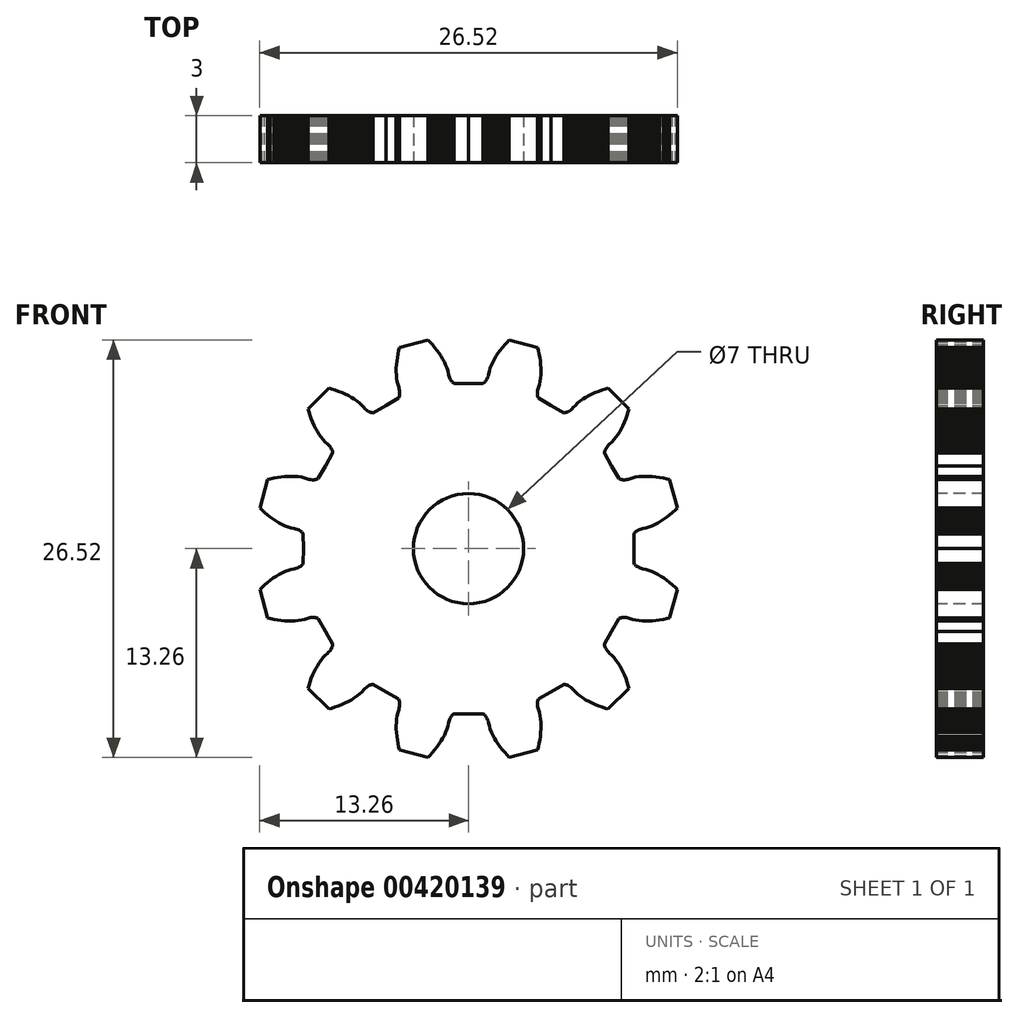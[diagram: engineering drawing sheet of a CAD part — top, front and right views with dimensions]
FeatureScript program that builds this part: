
annotation { "Feature Type Name" : "Feature", "Feature Type Description" : "" }
export const myFeature = defineFeature(function(context is Context, id is Id, definition is map)
    precondition{}
    {
        {
            var Q0;
            Q0=qCreatedBy(makeId("Front.planeOp"),FACE);
            var sketch = newSketch(context, id + "F0", { "sketchPlane" : qUnion([Q0])});
            skLineSegment(sketch, "E0", {"start": v(-10.5, 0) * mm, "end": v(-10.5, 0.93) * mm});
            skLineSegment(sketch, "E1", {"start": v(-10.5, 0.93) * mm, "end": v(-10.55, 1) * mm});
            skLineSegment(sketch, "E2", {"start": v(-10.55, 1) * mm, "end": v(-10.6, 1.05) * mm});
            skLineSegment(sketch, "E3", {"start": v(-10.6, 1.05) * mm, "end": v(-10.64, 1.09) * mm});
            skLineSegment(sketch, "E4", {"start": v(-10.64, 1.09) * mm, "end": v(-10.69, 1.12) * mm});
            skLineSegment(sketch, "E5", {"start": v(-10.69, 1.12) * mm, "end": v(-10.78, 1.17) * mm});
            skLineSegment(sketch, "E6", {"start": v(-10.78, 1.17) * mm, "end": v(-10.88, 1.22) * mm});
            skLineSegment(sketch, "E7", {"start": v(-10.88, 1.22) * mm, "end": v(-10.97, 1.25) * mm});
            skLineSegment(sketch, "E8", {"start": v(-10.97, 1.25) * mm, "end": v(-11.07, 1.28) * mm});
            skLineSegment(sketch, "E9", {"start": v(-11.07, 1.28) * mm, "end": v(-11.27, 1.32) * mm});
            skLineSegment(sketch, "E10", {"start": v(-11.27, 1.32) * mm, "end": v(-11.47, 1.38) * mm});
            skLineSegment(sketch, "E11", {"start": v(-11.47, 1.38) * mm, "end": v(-11.66, 1.45) * mm});
            skLineSegment(sketch, "E12", {"start": v(-11.66, 1.45) * mm, "end": v(-11.85, 1.54) * mm});
            skLineSegment(sketch, "E13", {"start": v(-11.85, 1.54) * mm, "end": v(-12.04, 1.64) * mm});
            skLineSegment(sketch, "E14", {"start": v(-12.04, 1.64) * mm, "end": v(-12.23, 1.76) * mm});
            skLineSegment(sketch, "E15", {"start": v(-12.23, 1.76) * mm, "end": v(-12.41, 1.88) * mm});
            skLineSegment(sketch, "E16", {"start": v(-12.41, 1.88) * mm, "end": v(-12.6, 2.01) * mm});
            skLineSegment(sketch, "E17", {"start": v(-12.6, 2.01) * mm, "end": v(-12.77, 2.15) * mm});
            skLineSegment(sketch, "E18", {"start": v(-12.77, 2.15) * mm, "end": v(-12.95, 2.3) * mm});
            skLineSegment(sketch, "E19", {"start": v(-12.95, 2.3) * mm, "end": v(-13.13, 2.46) * mm});
            skLineSegment(sketch, "E20", {"start": v(-13.13, 2.46) * mm, "end": v(-13.26, 2.58) * mm});
            skLineSegment(sketch, "E21", {"start": v(-13.26, 2.58) * mm, "end": v(-12.77, 4.4) * mm});
            skLineSegment(sketch, "E22", {"start": v(-12.77, 4.4) * mm, "end": v(-12.6, 4.43) * mm});
            skLineSegment(sketch, "E23", {"start": v(-12.6, 4.43) * mm, "end": v(-12.37, 4.48) * mm});
            skLineSegment(sketch, "E24", {"start": v(-12.37, 4.48) * mm, "end": v(-12.14, 4.52) * mm});
            skLineSegment(sketch, "E25", {"start": v(-12.14, 4.52) * mm, "end": v(-11.91, 4.56) * mm});
            skLineSegment(sketch, "E26", {"start": v(-11.91, 4.56) * mm, "end": v(-11.69, 4.58) * mm});
            skLineSegment(sketch, "E27", {"start": v(-11.69, 4.58) * mm, "end": v(-11.47, 4.6) * mm});
            skLineSegment(sketch, "E28", {"start": v(-11.47, 4.6) * mm, "end": v(-11.25, 4.6) * mm});
            skLineSegment(sketch, "E29", {"start": v(-11.25, 4.6) * mm, "end": v(-11.03, 4.59) * mm});
            skLineSegment(sketch, "E30", {"start": v(-11.03, 4.59) * mm, "end": v(-10.82, 4.57) * mm});
            skLineSegment(sketch, "E31", {"start": v(-10.82, 4.57) * mm, "end": v(-10.62, 4.54) * mm});
            skLineSegment(sketch, "E32", {"start": v(-10.62, 4.54) * mm, "end": v(-10.42, 4.5) * mm});
            skLineSegment(sketch, "E33", {"start": v(-10.42, 4.5) * mm, "end": v(-10.23, 4.43) * mm});
            skLineSegment(sketch, "E34", {"start": v(-10.23, 4.43) * mm, "end": v(-10.13, 4.4) * mm});
            skLineSegment(sketch, "E35", {"start": v(-10.13, 4.4) * mm, "end": v(-10.03, 4.38) * mm});
            skLineSegment(sketch, "E36", {"start": v(-10.03, 4.38) * mm, "end": v(-9.92, 4.37) * mm});
            skLineSegment(sketch, "E37", {"start": v(-9.92, 4.37) * mm, "end": v(-9.81, 4.37) * mm});
            skLineSegment(sketch, "E38", {"start": v(-9.81, 4.37) * mm, "end": v(-9.76, 4.38) * mm});
            skLineSegment(sketch, "E39", {"start": v(-9.76, 4.38) * mm, "end": v(-9.7, 4.39) * mm});
            skLineSegment(sketch, "E40", {"start": v(-9.7, 4.39) * mm, "end": v(-9.63, 4.4) * mm});
            skLineSegment(sketch, "E41", {"start": v(-9.63, 4.4) * mm, "end": v(-9.56, 4.44) * mm});
            skLineSegment(sketch, "E42", {"start": v(-9.56, 4.44) * mm, "end": v(-9.09, 5.25) * mm});
            skLineSegment(sketch, "E43", {"start": v(-9.09, 5.25) * mm, "end": v(-8.63, 6.06) * mm});
            skLineSegment(sketch, "E44", {"start": v(-8.63, 6.06) * mm, "end": v(-8.63, 6.14) * mm});
            skLineSegment(sketch, "E45", {"start": v(-8.63, 6.14) * mm, "end": v(-8.65, 6.2) * mm});
            skLineSegment(sketch, "E46", {"start": v(-8.65, 6.2) * mm, "end": v(-8.67, 6.26) * mm});
            skLineSegment(sketch, "E47", {"start": v(-8.67, 6.26) * mm, "end": v(-8.7, 6.31) * mm});
            skLineSegment(sketch, "E48", {"start": v(-8.7, 6.31) * mm, "end": v(-8.75, 6.4) * mm});
            skLineSegment(sketch, "E49", {"start": v(-8.75, 6.4) * mm, "end": v(-8.81, 6.5) * mm});
            skLineSegment(sketch, "E50", {"start": v(-8.81, 6.5) * mm, "end": v(-8.88, 6.57) * mm});
            skLineSegment(sketch, "E51", {"start": v(-8.88, 6.57) * mm, "end": v(-8.95, 6.64) * mm});
            skLineSegment(sketch, "E52", {"start": v(-8.95, 6.64) * mm, "end": v(-9.1, 6.78) * mm});
            skLineSegment(sketch, "E53", {"start": v(-9.1, 6.78) * mm, "end": v(-9.24, 6.92) * mm});
            skLineSegment(sketch, "E54", {"start": v(-9.24, 6.92) * mm, "end": v(-9.37, 7.09) * mm});
            skLineSegment(sketch, "E55", {"start": v(-9.37, 7.09) * mm, "end": v(-9.5, 7.26) * mm});
            skLineSegment(sketch, "E56", {"start": v(-9.5, 7.26) * mm, "end": v(-9.6, 7.44) * mm});
            skLineSegment(sketch, "E57", {"start": v(-9.6, 7.44) * mm, "end": v(-9.71, 7.63) * mm});
            skLineSegment(sketch, "E58", {"start": v(-9.71, 7.63) * mm, "end": v(-9.8, 7.83) * mm});
            skLineSegment(sketch, "E59", {"start": v(-9.8, 7.83) * mm, "end": v(-9.9, 8.04) * mm});
            skLineSegment(sketch, "E60", {"start": v(-9.9, 8.04) * mm, "end": v(-9.99, 8.25) * mm});
            skLineSegment(sketch, "E61", {"start": v(-9.99, 8.25) * mm, "end": v(-10.07, 8.47) * mm});
            skLineSegment(sketch, "E62", {"start": v(-10.07, 8.47) * mm, "end": v(-10.14, 8.7) * mm});
            skLineSegment(sketch, "E63", {"start": v(-10.14, 8.7) * mm, "end": v(-10.2, 8.87) * mm});
            skLineSegment(sketch, "E64", {"start": v(-10.2, 8.87) * mm, "end": v(-8.87, 10.2) * mm});
            skLineSegment(sketch, "E65", {"start": v(-8.87, 10.2) * mm, "end": v(-8.7, 10.14) * mm});
            skLineSegment(sketch, "E66", {"start": v(-8.7, 10.14) * mm, "end": v(-8.47, 10.07) * mm});
            skLineSegment(sketch, "E67", {"start": v(-8.47, 10.07) * mm, "end": v(-8.25, 9.99) * mm});
            skLineSegment(sketch, "E68", {"start": v(-8.25, 9.99) * mm, "end": v(-8.04, 9.9) * mm});
            skLineSegment(sketch, "E69", {"start": v(-8.04, 9.9) * mm, "end": v(-7.83, 9.8) * mm});
            skLineSegment(sketch, "E70", {"start": v(-7.83, 9.8) * mm, "end": v(-7.63, 9.71) * mm});
            skLineSegment(sketch, "E71", {"start": v(-7.63, 9.71) * mm, "end": v(-7.44, 9.6) * mm});
            skLineSegment(sketch, "E72", {"start": v(-7.44, 9.6) * mm, "end": v(-7.26, 9.5) * mm});
            skLineSegment(sketch, "E73", {"start": v(-7.26, 9.5) * mm, "end": v(-7.09, 9.37) * mm});
            skLineSegment(sketch, "E74", {"start": v(-7.09, 9.37) * mm, "end": v(-6.92, 9.24) * mm});
            skLineSegment(sketch, "E75", {"start": v(-6.92, 9.24) * mm, "end": v(-6.78, 9.1) * mm});
            skLineSegment(sketch, "E76", {"start": v(-6.78, 9.1) * mm, "end": v(-6.64, 8.95) * mm});
            skLineSegment(sketch, "E77", {"start": v(-6.64, 8.95) * mm, "end": v(-6.57, 8.88) * mm});
            skLineSegment(sketch, "E78", {"start": v(-6.57, 8.88) * mm, "end": v(-6.5, 8.81) * mm});
            skLineSegment(sketch, "E79", {"start": v(-6.5, 8.81) * mm, "end": v(-6.4, 8.75) * mm});
            skLineSegment(sketch, "E80", {"start": v(-6.4, 8.75) * mm, "end": v(-6.31, 8.7) * mm});
            skLineSegment(sketch, "E81", {"start": v(-6.31, 8.7) * mm, "end": v(-6.26, 8.67) * mm});
            skLineSegment(sketch, "E82", {"start": v(-6.26, 8.67) * mm, "end": v(-6.2, 8.65) * mm});
            skLineSegment(sketch, "E83", {"start": v(-6.2, 8.65) * mm, "end": v(-6.14, 8.63) * mm});
            skLineSegment(sketch, "E84", {"start": v(-6.14, 8.63) * mm, "end": v(-6.06, 8.63) * mm});
            skLineSegment(sketch, "E85", {"start": v(-6.06, 8.63) * mm, "end": v(-5.25, 9.09) * mm});
            skLineSegment(sketch, "E86", {"start": v(-5.25, 9.09) * mm, "end": v(-4.44, 9.56) * mm});
            skLineSegment(sketch, "E87", {"start": v(-4.44, 9.56) * mm, "end": v(-4.4, 9.63) * mm});
            skLineSegment(sketch, "E88", {"start": v(-4.4, 9.63) * mm, "end": v(-4.39, 9.7) * mm});
            skLineSegment(sketch, "E89", {"start": v(-4.39, 9.7) * mm, "end": v(-4.38, 9.76) * mm});
            skLineSegment(sketch, "E90", {"start": v(-4.38, 9.76) * mm, "end": v(-4.37, 9.81) * mm});
            skLineSegment(sketch, "E91", {"start": v(-4.37, 9.81) * mm, "end": v(-4.37, 9.92) * mm});
            skLineSegment(sketch, "E92", {"start": v(-4.37, 9.92) * mm, "end": v(-4.38, 10.03) * mm});
            skLineSegment(sketch, "E93", {"start": v(-4.38, 10.03) * mm, "end": v(-4.4, 10.13) * mm});
            skLineSegment(sketch, "E94", {"start": v(-4.4, 10.13) * mm, "end": v(-4.43, 10.23) * mm});
            skLineSegment(sketch, "E95", {"start": v(-4.43, 10.23) * mm, "end": v(-4.5, 10.42) * mm});
            skLineSegment(sketch, "E96", {"start": v(-4.5, 10.42) * mm, "end": v(-4.54, 10.62) * mm});
            skLineSegment(sketch, "E97", {"start": v(-4.54, 10.62) * mm, "end": v(-4.57, 10.82) * mm});
            skLineSegment(sketch, "E98", {"start": v(-4.57, 10.82) * mm, "end": v(-4.59, 11.03) * mm});
            skLineSegment(sketch, "E99", {"start": v(-4.59, 11.03) * mm, "end": v(-4.6, 11.25) * mm});
            skLineSegment(sketch, "E100", {"start": v(-4.6, 11.25) * mm, "end": v(-4.6, 11.47) * mm});
            skLineSegment(sketch, "E101", {"start": v(-4.6, 11.47) * mm, "end": v(-4.58, 11.69) * mm});
            skLineSegment(sketch, "E102", {"start": v(-4.58, 11.69) * mm, "end": v(-4.56, 11.91) * mm});
            skLineSegment(sketch, "E103", {"start": v(-4.56, 11.91) * mm, "end": v(-4.52, 12.14) * mm});
            skLineSegment(sketch, "E104", {"start": v(-4.52, 12.14) * mm, "end": v(-4.48, 12.37) * mm});
            skLineSegment(sketch, "E105", {"start": v(-4.48, 12.37) * mm, "end": v(-4.43, 12.6) * mm});
            skLineSegment(sketch, "E106", {"start": v(-4.43, 12.6) * mm, "end": v(-4.4, 12.77) * mm});
            skLineSegment(sketch, "E107", {"start": v(-4.4, 12.77) * mm, "end": v(-2.58, 13.26) * mm});
            skLineSegment(sketch, "E108", {"start": v(-2.58, 13.26) * mm, "end": v(-2.46, 13.13) * mm});
            skLineSegment(sketch, "E109", {"start": v(-2.46, 13.13) * mm, "end": v(-2.3, 12.95) * mm});
            skLineSegment(sketch, "E110", {"start": v(-2.3, 12.95) * mm, "end": v(-2.15, 12.77) * mm});
            skLineSegment(sketch, "E111", {"start": v(-2.15, 12.77) * mm, "end": v(-2.01, 12.6) * mm});
            skLineSegment(sketch, "E112", {"start": v(-2.01, 12.6) * mm, "end": v(-1.88, 12.41) * mm});
            skLineSegment(sketch, "E113", {"start": v(-1.88, 12.41) * mm, "end": v(-1.76, 12.23) * mm});
            skLineSegment(sketch, "E114", {"start": v(-1.76, 12.23) * mm, "end": v(-1.64, 12.04) * mm});
            skLineSegment(sketch, "E115", {"start": v(-1.64, 12.04) * mm, "end": v(-1.54, 11.85) * mm});
            skLineSegment(sketch, "E116", {"start": v(-1.54, 11.85) * mm, "end": v(-1.45, 11.66) * mm});
            skLineSegment(sketch, "E117", {"start": v(-1.45, 11.66) * mm, "end": v(-1.38, 11.47) * mm});
            skLineSegment(sketch, "E118", {"start": v(-1.38, 11.47) * mm, "end": v(-1.32, 11.27) * mm});
            skLineSegment(sketch, "E119", {"start": v(-1.32, 11.27) * mm, "end": v(-1.28, 11.07) * mm});
            skLineSegment(sketch, "E120", {"start": v(-1.28, 11.07) * mm, "end": v(-1.25, 10.97) * mm});
            skLineSegment(sketch, "E121", {"start": v(-1.25, 10.97) * mm, "end": v(-1.22, 10.88) * mm});
            skLineSegment(sketch, "E122", {"start": v(-1.22, 10.88) * mm, "end": v(-1.17, 10.78) * mm});
            skLineSegment(sketch, "E123", {"start": v(-1.17, 10.78) * mm, "end": v(-1.12, 10.69) * mm});
            skLineSegment(sketch, "E124", {"start": v(-1.12, 10.69) * mm, "end": v(-1.09, 10.64) * mm});
            skLineSegment(sketch, "E125", {"start": v(-1.09, 10.64) * mm, "end": v(-1.05, 10.6) * mm});
            skLineSegment(sketch, "E126", {"start": v(-1.05, 10.6) * mm, "end": v(-1, 10.55) * mm});
            skLineSegment(sketch, "E127", {"start": v(-1, 10.55) * mm, "end": v(-0.93, 10.5) * mm});
            skLineSegment(sketch, "E128", {"start": v(-0.93, 10.5) * mm, "end": v(0, 10.5) * mm});
            skLineSegment(sketch, "E129", {"start": v(0, 10.5) * mm, "end": v(0.93, 10.5) * mm});
            skLineSegment(sketch, "E130", {"start": v(0.93, 10.5) * mm, "end": v(1, 10.55) * mm});
            skLineSegment(sketch, "E131", {"start": v(1, 10.55) * mm, "end": v(1.05, 10.6) * mm});
            skLineSegment(sketch, "E132", {"start": v(1.05, 10.6) * mm, "end": v(1.09, 10.64) * mm});
            skLineSegment(sketch, "E133", {"start": v(1.09, 10.64) * mm, "end": v(1.12, 10.69) * mm});
            skLineSegment(sketch, "E134", {"start": v(1.12, 10.69) * mm, "end": v(1.17, 10.78) * mm});
            skLineSegment(sketch, "E135", {"start": v(1.17, 10.78) * mm, "end": v(1.22, 10.88) * mm});
            skLineSegment(sketch, "E136", {"start": v(1.22, 10.88) * mm, "end": v(1.25, 10.97) * mm});
            skLineSegment(sketch, "E137", {"start": v(1.25, 10.97) * mm, "end": v(1.28, 11.07) * mm});
            skLineSegment(sketch, "E138", {"start": v(1.28, 11.07) * mm, "end": v(1.32, 11.27) * mm});
            skLineSegment(sketch, "E139", {"start": v(1.32, 11.27) * mm, "end": v(1.38, 11.47) * mm});
            skLineSegment(sketch, "E140", {"start": v(1.38, 11.47) * mm, "end": v(1.45, 11.66) * mm});
            skLineSegment(sketch, "E141", {"start": v(1.45, 11.66) * mm, "end": v(1.54, 11.85) * mm});
            skLineSegment(sketch, "E142", {"start": v(1.54, 11.85) * mm, "end": v(1.64, 12.04) * mm});
            skLineSegment(sketch, "E143", {"start": v(1.64, 12.04) * mm, "end": v(1.76, 12.23) * mm});
            skLineSegment(sketch, "E144", {"start": v(1.76, 12.23) * mm, "end": v(1.88, 12.41) * mm});
            skLineSegment(sketch, "E145", {"start": v(1.88, 12.41) * mm, "end": v(2.01, 12.6) * mm});
            skLineSegment(sketch, "E146", {"start": v(2.01, 12.6) * mm, "end": v(2.15, 12.77) * mm});
            skLineSegment(sketch, "E147", {"start": v(2.15, 12.77) * mm, "end": v(2.3, 12.95) * mm});
            skLineSegment(sketch, "E148", {"start": v(2.3, 12.95) * mm, "end": v(2.46, 13.13) * mm});
            skLineSegment(sketch, "E149", {"start": v(2.46, 13.13) * mm, "end": v(2.58, 13.26) * mm});
            skLineSegment(sketch, "E150", {"start": v(2.58, 13.26) * mm, "end": v(4.4, 12.77) * mm});
            skLineSegment(sketch, "E151", {"start": v(4.4, 12.77) * mm, "end": v(4.43, 12.6) * mm});
            skLineSegment(sketch, "E152", {"start": v(4.43, 12.6) * mm, "end": v(4.48, 12.37) * mm});
            skLineSegment(sketch, "E153", {"start": v(4.48, 12.37) * mm, "end": v(4.52, 12.14) * mm});
            skLineSegment(sketch, "E154", {"start": v(4.52, 12.14) * mm, "end": v(4.56, 11.91) * mm});
            skLineSegment(sketch, "E155", {"start": v(4.56, 11.91) * mm, "end": v(4.58, 11.69) * mm});
            skLineSegment(sketch, "E156", {"start": v(4.58, 11.69) * mm, "end": v(4.6, 11.47) * mm});
            skLineSegment(sketch, "E157", {"start": v(4.6, 11.47) * mm, "end": v(4.6, 11.25) * mm});
            skLineSegment(sketch, "E158", {"start": v(4.6, 11.25) * mm, "end": v(4.59, 11.03) * mm});
            skLineSegment(sketch, "E159", {"start": v(4.59, 11.03) * mm, "end": v(4.57, 10.82) * mm});
            skLineSegment(sketch, "E160", {"start": v(4.57, 10.82) * mm, "end": v(4.54, 10.62) * mm});
            skLineSegment(sketch, "E161", {"start": v(4.54, 10.62) * mm, "end": v(4.5, 10.42) * mm});
            skLineSegment(sketch, "E162", {"start": v(4.5, 10.42) * mm, "end": v(4.43, 10.23) * mm});
            skLineSegment(sketch, "E163", {"start": v(4.43, 10.23) * mm, "end": v(4.4, 10.13) * mm});
            skLineSegment(sketch, "E164", {"start": v(4.4, 10.13) * mm, "end": v(4.38, 10.03) * mm});
            skLineSegment(sketch, "E165", {"start": v(4.38, 10.03) * mm, "end": v(4.37, 9.92) * mm});
            skLineSegment(sketch, "E166", {"start": v(4.37, 9.92) * mm, "end": v(4.37, 9.81) * mm});
            skLineSegment(sketch, "E167", {"start": v(4.37, 9.81) * mm, "end": v(4.38, 9.76) * mm});
            skLineSegment(sketch, "E168", {"start": v(4.38, 9.76) * mm, "end": v(4.39, 9.7) * mm});
            skLineSegment(sketch, "E169", {"start": v(4.39, 9.7) * mm, "end": v(4.4, 9.63) * mm});
            skLineSegment(sketch, "E170", {"start": v(4.4, 9.63) * mm, "end": v(4.44, 9.56) * mm});
            skLineSegment(sketch, "E171", {"start": v(4.44, 9.56) * mm, "end": v(5.25, 9.09) * mm});
            skLineSegment(sketch, "E172", {"start": v(5.25, 9.09) * mm, "end": v(6.06, 8.63) * mm});
            skLineSegment(sketch, "E173", {"start": v(6.06, 8.63) * mm, "end": v(6.14, 8.63) * mm});
            skLineSegment(sketch, "E174", {"start": v(6.14, 8.63) * mm, "end": v(6.2, 8.65) * mm});
            skLineSegment(sketch, "E175", {"start": v(6.2, 8.65) * mm, "end": v(6.26, 8.67) * mm});
            skLineSegment(sketch, "E176", {"start": v(6.26, 8.67) * mm, "end": v(6.31, 8.7) * mm});
            skLineSegment(sketch, "E177", {"start": v(6.31, 8.7) * mm, "end": v(6.4, 8.75) * mm});
            skLineSegment(sketch, "E178", {"start": v(6.4, 8.75) * mm, "end": v(6.5, 8.81) * mm});
            skLineSegment(sketch, "E179", {"start": v(6.5, 8.81) * mm, "end": v(6.57, 8.88) * mm});
            skLineSegment(sketch, "E180", {"start": v(6.57, 8.88) * mm, "end": v(6.64, 8.95) * mm});
            skLineSegment(sketch, "E181", {"start": v(6.64, 8.95) * mm, "end": v(6.78, 9.1) * mm});
            skLineSegment(sketch, "E182", {"start": v(6.78, 9.1) * mm, "end": v(6.92, 9.24) * mm});
            skLineSegment(sketch, "E183", {"start": v(6.92, 9.24) * mm, "end": v(7.09, 9.37) * mm});
            skLineSegment(sketch, "E184", {"start": v(7.09, 9.37) * mm, "end": v(7.26, 9.5) * mm});
            skLineSegment(sketch, "E185", {"start": v(7.26, 9.5) * mm, "end": v(7.44, 9.6) * mm});
            skLineSegment(sketch, "E186", {"start": v(7.44, 9.6) * mm, "end": v(7.63, 9.71) * mm});
            skLineSegment(sketch, "E187", {"start": v(7.63, 9.71) * mm, "end": v(7.83, 9.8) * mm});
            skLineSegment(sketch, "E188", {"start": v(7.83, 9.8) * mm, "end": v(8.04, 9.9) * mm});
            skLineSegment(sketch, "E189", {"start": v(8.04, 9.9) * mm, "end": v(8.25, 9.99) * mm});
            skLineSegment(sketch, "E190", {"start": v(8.25, 9.99) * mm, "end": v(8.47, 10.07) * mm});
            skLineSegment(sketch, "E191", {"start": v(8.47, 10.07) * mm, "end": v(8.7, 10.14) * mm});
            skLineSegment(sketch, "E192", {"start": v(8.7, 10.14) * mm, "end": v(8.87, 10.2) * mm});
            skLineSegment(sketch, "E193", {"start": v(8.87, 10.2) * mm, "end": v(10.19, 8.87) * mm});
            skLineSegment(sketch, "E194", {"start": v(10.19, 8.87) * mm, "end": v(10.14, 8.7) * mm});
            skLineSegment(sketch, "E195", {"start": v(10.14, 8.7) * mm, "end": v(10.07, 8.47) * mm});
            skLineSegment(sketch, "E196", {"start": v(10.07, 8.47) * mm, "end": v(9.99, 8.25) * mm});
            skLineSegment(sketch, "E197", {"start": v(9.99, 8.25) * mm, "end": v(9.9, 8.04) * mm});
            skLineSegment(sketch, "E198", {"start": v(9.9, 8.04) * mm, "end": v(9.8, 7.83) * mm});
            skLineSegment(sketch, "E199", {"start": v(9.8, 7.83) * mm, "end": v(9.71, 7.63) * mm});
            skLineSegment(sketch, "E200", {"start": v(9.71, 7.63) * mm, "end": v(9.6, 7.44) * mm});
            skLineSegment(sketch, "E201", {"start": v(9.6, 7.44) * mm, "end": v(9.5, 7.26) * mm});
            skLineSegment(sketch, "E202", {"start": v(9.5, 7.26) * mm, "end": v(9.37, 7.09) * mm});
            skLineSegment(sketch, "E203", {"start": v(9.37, 7.09) * mm, "end": v(9.24, 6.92) * mm});
            skLineSegment(sketch, "E204", {"start": v(9.24, 6.92) * mm, "end": v(9.1, 6.78) * mm});
            skLineSegment(sketch, "E205", {"start": v(9.1, 6.78) * mm, "end": v(8.95, 6.64) * mm});
            skLineSegment(sketch, "E206", {"start": v(8.95, 6.64) * mm, "end": v(8.88, 6.57) * mm});
            skLineSegment(sketch, "E207", {"start": v(8.88, 6.57) * mm, "end": v(8.81, 6.5) * mm});
            skLineSegment(sketch, "E208", {"start": v(8.81, 6.5) * mm, "end": v(8.75, 6.4) * mm});
            skLineSegment(sketch, "E209", {"start": v(8.75, 6.4) * mm, "end": v(8.7, 6.31) * mm});
            skLineSegment(sketch, "E210", {"start": v(8.7, 6.31) * mm, "end": v(8.67, 6.26) * mm});
            skLineSegment(sketch, "E211", {"start": v(8.67, 6.26) * mm, "end": v(8.65, 6.2) * mm});
            skLineSegment(sketch, "E212", {"start": v(8.65, 6.2) * mm, "end": v(8.63, 6.14) * mm});
            skLineSegment(sketch, "E213", {"start": v(8.63, 6.14) * mm, "end": v(8.63, 6.06) * mm});
            skLineSegment(sketch, "E214", {"start": v(8.63, 6.06) * mm, "end": v(9.09, 5.25) * mm});
            skLineSegment(sketch, "E215", {"start": v(9.09, 5.25) * mm, "end": v(9.56, 4.44) * mm});
            skLineSegment(sketch, "E216", {"start": v(9.56, 4.44) * mm, "end": v(9.63, 4.4) * mm});
            skLineSegment(sketch, "E217", {"start": v(9.63, 4.4) * mm, "end": v(9.7, 4.39) * mm});
            skLineSegment(sketch, "E218", {"start": v(9.7, 4.39) * mm, "end": v(9.76, 4.38) * mm});
            skLineSegment(sketch, "E219", {"start": v(9.76, 4.38) * mm, "end": v(9.81, 4.37) * mm});
            skLineSegment(sketch, "E220", {"start": v(9.81, 4.37) * mm, "end": v(9.92, 4.37) * mm});
            skLineSegment(sketch, "E221", {"start": v(9.92, 4.37) * mm, "end": v(10.03, 4.38) * mm});
            skLineSegment(sketch, "E222", {"start": v(10.03, 4.38) * mm, "end": v(10.13, 4.4) * mm});
            skLineSegment(sketch, "E223", {"start": v(10.13, 4.4) * mm, "end": v(10.23, 4.43) * mm});
            skLineSegment(sketch, "E224", {"start": v(10.23, 4.43) * mm, "end": v(10.42, 4.5) * mm});
            skLineSegment(sketch, "E225", {"start": v(10.42, 4.5) * mm, "end": v(10.62, 4.54) * mm});
            skLineSegment(sketch, "E226", {"start": v(10.62, 4.54) * mm, "end": v(10.82, 4.57) * mm});
            skLineSegment(sketch, "E227", {"start": v(10.82, 4.57) * mm, "end": v(11.03, 4.59) * mm});
            skLineSegment(sketch, "E228", {"start": v(11.03, 4.59) * mm, "end": v(11.25, 4.6) * mm});
            skLineSegment(sketch, "E229", {"start": v(11.25, 4.6) * mm, "end": v(11.47, 4.6) * mm});
            skLineSegment(sketch, "E230", {"start": v(11.47, 4.6) * mm, "end": v(11.69, 4.58) * mm});
            skLineSegment(sketch, "E231", {"start": v(11.69, 4.58) * mm, "end": v(11.91, 4.56) * mm});
            skLineSegment(sketch, "E232", {"start": v(11.91, 4.56) * mm, "end": v(12.14, 4.52) * mm});
            skLineSegment(sketch, "E233", {"start": v(12.14, 4.52) * mm, "end": v(12.37, 4.48) * mm});
            skLineSegment(sketch, "E234", {"start": v(12.37, 4.48) * mm, "end": v(12.6, 4.43) * mm});
            skLineSegment(sketch, "E235", {"start": v(12.6, 4.43) * mm, "end": v(12.77, 4.4) * mm});
            skLineSegment(sketch, "E236", {"start": v(12.77, 4.4) * mm, "end": v(13.26, 2.58) * mm});
            skLineSegment(sketch, "E237", {"start": v(13.26, 2.58) * mm, "end": v(13.13, 2.46) * mm});
            skLineSegment(sketch, "E238", {"start": v(13.13, 2.46) * mm, "end": v(12.95, 2.3) * mm});
            skLineSegment(sketch, "E239", {"start": v(12.95, 2.3) * mm, "end": v(12.77, 2.15) * mm});
            skLineSegment(sketch, "E240", {"start": v(12.77, 2.15) * mm, "end": v(12.6, 2.01) * mm});
            skLineSegment(sketch, "E241", {"start": v(12.6, 2.01) * mm, "end": v(12.41, 1.88) * mm});
            skLineSegment(sketch, "E242", {"start": v(12.41, 1.88) * mm, "end": v(12.23, 1.76) * mm});
            skLineSegment(sketch, "E243", {"start": v(12.23, 1.76) * mm, "end": v(12.04, 1.64) * mm});
            skLineSegment(sketch, "E244", {"start": v(12.04, 1.64) * mm, "end": v(11.85, 1.54) * mm});
            skLineSegment(sketch, "E245", {"start": v(11.85, 1.54) * mm, "end": v(11.66, 1.45) * mm});
            skLineSegment(sketch, "E246", {"start": v(11.66, 1.45) * mm, "end": v(11.47, 1.38) * mm});
            skLineSegment(sketch, "E247", {"start": v(11.47, 1.38) * mm, "end": v(11.27, 1.32) * mm});
            skLineSegment(sketch, "E248", {"start": v(11.27, 1.32) * mm, "end": v(11.07, 1.28) * mm});
            skLineSegment(sketch, "E249", {"start": v(11.07, 1.28) * mm, "end": v(10.97, 1.25) * mm});
            skLineSegment(sketch, "E250", {"start": v(10.97, 1.25) * mm, "end": v(10.88, 1.22) * mm});
            skLineSegment(sketch, "E251", {"start": v(10.88, 1.22) * mm, "end": v(10.78, 1.17) * mm});
            skLineSegment(sketch, "E252", {"start": v(10.78, 1.17) * mm, "end": v(10.69, 1.12) * mm});
            skLineSegment(sketch, "E253", {"start": v(10.69, 1.12) * mm, "end": v(10.64, 1.09) * mm});
            skLineSegment(sketch, "E254", {"start": v(10.64, 1.09) * mm, "end": v(10.6, 1.05) * mm});
            skLineSegment(sketch, "E255", {"start": v(10.6, 1.05) * mm, "end": v(10.55, 1) * mm});
            skLineSegment(sketch, "E256", {"start": v(10.55, 1) * mm, "end": v(10.5, 0.93) * mm});
            skLineSegment(sketch, "E257", {"start": v(10.5, 0.93) * mm, "end": v(10.5, 0) * mm});
            skLineSegment(sketch, "E258", {"start": v(10.5, 0) * mm, "end": v(10.5, -0.93) * mm});
            skLineSegment(sketch, "E259", {"start": v(10.5, -0.93) * mm, "end": v(10.55, -1) * mm});
            skLineSegment(sketch, "E260", {"start": v(10.55, -1) * mm, "end": v(10.6, -1.05) * mm});
            skLineSegment(sketch, "E261", {"start": v(10.6, -1.05) * mm, "end": v(10.64, -1.09) * mm});
            skLineSegment(sketch, "E262", {"start": v(10.64, -1.09) * mm, "end": v(10.69, -1.12) * mm});
            skLineSegment(sketch, "E263", {"start": v(10.69, -1.12) * mm, "end": v(10.78, -1.17) * mm});
            skLineSegment(sketch, "E264", {"start": v(10.78, -1.17) * mm, "end": v(10.88, -1.22) * mm});
            skLineSegment(sketch, "E265", {"start": v(10.88, -1.22) * mm, "end": v(10.97, -1.25) * mm});
            skLineSegment(sketch, "E266", {"start": v(10.97, -1.25) * mm, "end": v(11.07, -1.28) * mm});
            skLineSegment(sketch, "E267", {"start": v(11.07, -1.28) * mm, "end": v(11.27, -1.32) * mm});
            skLineSegment(sketch, "E268", {"start": v(11.27, -1.32) * mm, "end": v(11.47, -1.38) * mm});
            skLineSegment(sketch, "E269", {"start": v(11.47, -1.38) * mm, "end": v(11.66, -1.45) * mm});
            skLineSegment(sketch, "E270", {"start": v(11.66, -1.45) * mm, "end": v(11.85, -1.54) * mm});
            skLineSegment(sketch, "E271", {"start": v(11.85, -1.54) * mm, "end": v(12.04, -1.64) * mm});
            skLineSegment(sketch, "E272", {"start": v(12.04, -1.64) * mm, "end": v(12.23, -1.76) * mm});
            skLineSegment(sketch, "E273", {"start": v(12.23, -1.76) * mm, "end": v(12.41, -1.88) * mm});
            skLineSegment(sketch, "E274", {"start": v(12.41, -1.88) * mm, "end": v(12.6, -2.01) * mm});
            skLineSegment(sketch, "E275", {"start": v(12.6, -2.01) * mm, "end": v(12.77, -2.15) * mm});
            skLineSegment(sketch, "E276", {"start": v(12.77, -2.15) * mm, "end": v(12.95, -2.3) * mm});
            skLineSegment(sketch, "E277", {"start": v(12.95, -2.3) * mm, "end": v(13.13, -2.46) * mm});
            skLineSegment(sketch, "E278", {"start": v(13.13, -2.46) * mm, "end": v(13.26, -2.58) * mm});
            skLineSegment(sketch, "E279", {"start": v(13.26, -2.58) * mm, "end": v(12.77, -4.4) * mm});
            skLineSegment(sketch, "E280", {"start": v(12.77, -4.4) * mm, "end": v(12.6, -4.43) * mm});
            skLineSegment(sketch, "E281", {"start": v(12.6, -4.43) * mm, "end": v(12.37, -4.48) * mm});
            skLineSegment(sketch, "E282", {"start": v(12.37, -4.48) * mm, "end": v(12.14, -4.52) * mm});
            skLineSegment(sketch, "E283", {"start": v(12.14, -4.52) * mm, "end": v(11.91, -4.56) * mm});
            skLineSegment(sketch, "E284", {"start": v(11.91, -4.56) * mm, "end": v(11.69, -4.58) * mm});
            skLineSegment(sketch, "E285", {"start": v(11.69, -4.58) * mm, "end": v(11.47, -4.6) * mm});
            skLineSegment(sketch, "E286", {"start": v(11.47, -4.6) * mm, "end": v(11.25, -4.6) * mm});
            skLineSegment(sketch, "E287", {"start": v(11.25, -4.6) * mm, "end": v(11.03, -4.59) * mm});
            skLineSegment(sketch, "E288", {"start": v(11.03, -4.59) * mm, "end": v(10.82, -4.57) * mm});
            skLineSegment(sketch, "E289", {"start": v(10.82, -4.57) * mm, "end": v(10.62, -4.54) * mm});
            skLineSegment(sketch, "E290", {"start": v(10.62, -4.54) * mm, "end": v(10.42, -4.5) * mm});
            skLineSegment(sketch, "E291", {"start": v(10.42, -4.5) * mm, "end": v(10.23, -4.43) * mm});
            skLineSegment(sketch, "E292", {"start": v(10.23, -4.43) * mm, "end": v(10.13, -4.4) * mm});
            skLineSegment(sketch, "E293", {"start": v(10.13, -4.4) * mm, "end": v(10.03, -4.38) * mm});
            skLineSegment(sketch, "E294", {"start": v(10.03, -4.38) * mm, "end": v(9.92, -4.37) * mm});
            skLineSegment(sketch, "E295", {"start": v(9.92, -4.37) * mm, "end": v(9.81, -4.37) * mm});
            skLineSegment(sketch, "E296", {"start": v(9.81, -4.37) * mm, "end": v(9.76, -4.38) * mm});
            skLineSegment(sketch, "E297", {"start": v(9.76, -4.38) * mm, "end": v(9.7, -4.39) * mm});
            skLineSegment(sketch, "E298", {"start": v(9.7, -4.39) * mm, "end": v(9.63, -4.4) * mm});
            skLineSegment(sketch, "E299", {"start": v(9.63, -4.4) * mm, "end": v(9.56, -4.44) * mm});
            skLineSegment(sketch, "E300", {"start": v(9.56, -4.44) * mm, "end": v(9.09, -5.25) * mm});
            skLineSegment(sketch, "E301", {"start": v(9.09, -5.25) * mm, "end": v(8.63, -6.06) * mm});
            skLineSegment(sketch, "E302", {"start": v(8.63, -6.06) * mm, "end": v(8.63, -6.14) * mm});
            skLineSegment(sketch, "E303", {"start": v(8.63, -6.14) * mm, "end": v(8.65, -6.2) * mm});
            skLineSegment(sketch, "E304", {"start": v(8.65, -6.2) * mm, "end": v(8.67, -6.26) * mm});
            skLineSegment(sketch, "E305", {"start": v(8.67, -6.26) * mm, "end": v(8.7, -6.31) * mm});
            skLineSegment(sketch, "E306", {"start": v(8.7, -6.31) * mm, "end": v(8.75, -6.4) * mm});
            skLineSegment(sketch, "E307", {"start": v(8.75, -6.4) * mm, "end": v(8.81, -6.5) * mm});
            skLineSegment(sketch, "E308", {"start": v(8.81, -6.5) * mm, "end": v(8.88, -6.57) * mm});
            skLineSegment(sketch, "E309", {"start": v(8.88, -6.57) * mm, "end": v(8.95, -6.64) * mm});
            skLineSegment(sketch, "E310", {"start": v(8.95, -6.64) * mm, "end": v(9.1, -6.78) * mm});
            skLineSegment(sketch, "E311", {"start": v(9.1, -6.78) * mm, "end": v(9.24, -6.92) * mm});
            skLineSegment(sketch, "E312", {"start": v(9.24, -6.92) * mm, "end": v(9.37, -7.09) * mm});
            skLineSegment(sketch, "E313", {"start": v(9.37, -7.09) * mm, "end": v(9.5, -7.26) * mm});
            skLineSegment(sketch, "E314", {"start": v(9.5, -7.26) * mm, "end": v(9.6, -7.44) * mm});
            skLineSegment(sketch, "E315", {"start": v(9.6, -7.44) * mm, "end": v(9.71, -7.63) * mm});
            skLineSegment(sketch, "E316", {"start": v(9.71, -7.63) * mm, "end": v(9.8, -7.83) * mm});
            skLineSegment(sketch, "E317", {"start": v(9.8, -7.83) * mm, "end": v(9.9, -8.04) * mm});
            skLineSegment(sketch, "E318", {"start": v(9.9, -8.04) * mm, "end": v(9.99, -8.25) * mm});
            skLineSegment(sketch, "E319", {"start": v(9.99, -8.25) * mm, "end": v(10.07, -8.47) * mm});
            skLineSegment(sketch, "E320", {"start": v(10.07, -8.47) * mm, "end": v(10.14, -8.7) * mm});
            skLineSegment(sketch, "E321", {"start": v(10.14, -8.7) * mm, "end": v(10.19, -8.87) * mm});
            skLineSegment(sketch, "E322", {"start": v(10.19, -8.87) * mm, "end": v(8.87, -10.19) * mm});
            skLineSegment(sketch, "E323", {"start": v(8.87, -10.19) * mm, "end": v(8.7, -10.14) * mm});
            skLineSegment(sketch, "E324", {"start": v(8.7, -10.14) * mm, "end": v(8.47, -10.07) * mm});
            skLineSegment(sketch, "E325", {"start": v(8.47, -10.07) * mm, "end": v(8.25, -9.99) * mm});
            skLineSegment(sketch, "E326", {"start": v(8.25, -9.99) * mm, "end": v(8.04, -9.9) * mm});
            skLineSegment(sketch, "E327", {"start": v(8.04, -9.9) * mm, "end": v(7.83, -9.8) * mm});
            skLineSegment(sketch, "E328", {"start": v(7.83, -9.8) * mm, "end": v(7.63, -9.71) * mm});
            skLineSegment(sketch, "E329", {"start": v(7.63, -9.71) * mm, "end": v(7.44, -9.6) * mm});
            skLineSegment(sketch, "E330", {"start": v(7.44, -9.6) * mm, "end": v(7.26, -9.5) * mm});
            skLineSegment(sketch, "E331", {"start": v(7.26, -9.5) * mm, "end": v(7.09, -9.37) * mm});
            skLineSegment(sketch, "E332", {"start": v(7.09, -9.37) * mm, "end": v(6.92, -9.24) * mm});
            skLineSegment(sketch, "E333", {"start": v(6.92, -9.24) * mm, "end": v(6.78, -9.1) * mm});
            skLineSegment(sketch, "E334", {"start": v(6.78, -9.1) * mm, "end": v(6.64, -8.95) * mm});
            skLineSegment(sketch, "E335", {"start": v(6.64, -8.95) * mm, "end": v(6.57, -8.88) * mm});
            skLineSegment(sketch, "E336", {"start": v(6.57, -8.88) * mm, "end": v(6.5, -8.81) * mm});
            skLineSegment(sketch, "E337", {"start": v(6.5, -8.81) * mm, "end": v(6.4, -8.75) * mm});
            skLineSegment(sketch, "E338", {"start": v(6.4, -8.75) * mm, "end": v(6.31, -8.7) * mm});
            skLineSegment(sketch, "E339", {"start": v(6.31, -8.7) * mm, "end": v(6.26, -8.67) * mm});
            skLineSegment(sketch, "E340", {"start": v(6.26, -8.67) * mm, "end": v(6.2, -8.65) * mm});
            skLineSegment(sketch, "E341", {"start": v(6.2, -8.65) * mm, "end": v(6.14, -8.63) * mm});
            skLineSegment(sketch, "E342", {"start": v(6.14, -8.63) * mm, "end": v(6.06, -8.63) * mm});
            skLineSegment(sketch, "E343", {"start": v(6.06, -8.63) * mm, "end": v(5.25, -9.09) * mm});
            skLineSegment(sketch, "E344", {"start": v(5.25, -9.09) * mm, "end": v(4.44, -9.56) * mm});
            skLineSegment(sketch, "E345", {"start": v(4.44, -9.56) * mm, "end": v(4.4, -9.63) * mm});
            skLineSegment(sketch, "E346", {"start": v(4.4, -9.63) * mm, "end": v(4.39, -9.7) * mm});
            skLineSegment(sketch, "E347", {"start": v(4.39, -9.7) * mm, "end": v(4.38, -9.76) * mm});
            skLineSegment(sketch, "E348", {"start": v(4.38, -9.76) * mm, "end": v(4.37, -9.81) * mm});
            skLineSegment(sketch, "E349", {"start": v(4.37, -9.81) * mm, "end": v(4.37, -9.92) * mm});
            skLineSegment(sketch, "E350", {"start": v(4.37, -9.92) * mm, "end": v(4.38, -10.03) * mm});
            skLineSegment(sketch, "E351", {"start": v(4.38, -10.03) * mm, "end": v(4.4, -10.13) * mm});
            skLineSegment(sketch, "E352", {"start": v(4.4, -10.13) * mm, "end": v(4.43, -10.23) * mm});
            skLineSegment(sketch, "E353", {"start": v(4.43, -10.23) * mm, "end": v(4.5, -10.42) * mm});
            skLineSegment(sketch, "E354", {"start": v(4.5, -10.42) * mm, "end": v(4.54, -10.62) * mm});
            skLineSegment(sketch, "E355", {"start": v(4.54, -10.62) * mm, "end": v(4.57, -10.82) * mm});
            skLineSegment(sketch, "E356", {"start": v(4.57, -10.82) * mm, "end": v(4.59, -11.03) * mm});
            skLineSegment(sketch, "E357", {"start": v(4.59, -11.03) * mm, "end": v(4.6, -11.25) * mm});
            skLineSegment(sketch, "E358", {"start": v(4.6, -11.25) * mm, "end": v(4.6, -11.47) * mm});
            skLineSegment(sketch, "E359", {"start": v(4.6, -11.47) * mm, "end": v(4.58, -11.69) * mm});
            skLineSegment(sketch, "E360", {"start": v(4.58, -11.69) * mm, "end": v(4.56, -11.91) * mm});
            skLineSegment(sketch, "E361", {"start": v(4.56, -11.91) * mm, "end": v(4.52, -12.14) * mm});
            skLineSegment(sketch, "E362", {"start": v(4.52, -12.14) * mm, "end": v(4.48, -12.37) * mm});
            skLineSegment(sketch, "E363", {"start": v(4.48, -12.37) * mm, "end": v(4.43, -12.6) * mm});
            skLineSegment(sketch, "E364", {"start": v(4.43, -12.6) * mm, "end": v(4.4, -12.77) * mm});
            skLineSegment(sketch, "E365", {"start": v(4.4, -12.77) * mm, "end": v(2.58, -13.26) * mm});
            skLineSegment(sketch, "E366", {"start": v(2.58, -13.26) * mm, "end": v(2.46, -13.13) * mm});
            skLineSegment(sketch, "E367", {"start": v(2.46, -13.13) * mm, "end": v(2.3, -12.95) * mm});
            skLineSegment(sketch, "E368", {"start": v(2.3, -12.95) * mm, "end": v(2.15, -12.77) * mm});
            skLineSegment(sketch, "E369", {"start": v(2.15, -12.77) * mm, "end": v(2.01, -12.6) * mm});
            skLineSegment(sketch, "E370", {"start": v(2.01, -12.6) * mm, "end": v(1.88, -12.41) * mm});
            skLineSegment(sketch, "E371", {"start": v(1.88, -12.41) * mm, "end": v(1.76, -12.23) * mm});
            skLineSegment(sketch, "E372", {"start": v(1.76, -12.23) * mm, "end": v(1.64, -12.04) * mm});
            skLineSegment(sketch, "E373", {"start": v(1.64, -12.04) * mm, "end": v(1.54, -11.85) * mm});
            skLineSegment(sketch, "E374", {"start": v(1.54, -11.85) * mm, "end": v(1.45, -11.66) * mm});
            skLineSegment(sketch, "E375", {"start": v(1.45, -11.66) * mm, "end": v(1.38, -11.47) * mm});
            skLineSegment(sketch, "E376", {"start": v(1.38, -11.47) * mm, "end": v(1.32, -11.27) * mm});
            skLineSegment(sketch, "E377", {"start": v(1.32, -11.27) * mm, "end": v(1.28, -11.07) * mm});
            skLineSegment(sketch, "E378", {"start": v(1.28, -11.07) * mm, "end": v(1.25, -10.97) * mm});
            skLineSegment(sketch, "E379", {"start": v(1.25, -10.97) * mm, "end": v(1.22, -10.88) * mm});
            skLineSegment(sketch, "E380", {"start": v(1.22, -10.88) * mm, "end": v(1.17, -10.78) * mm});
            skLineSegment(sketch, "E381", {"start": v(1.17, -10.78) * mm, "end": v(1.12, -10.69) * mm});
            skLineSegment(sketch, "E382", {"start": v(1.12, -10.69) * mm, "end": v(1.09, -10.64) * mm});
            skLineSegment(sketch, "E383", {"start": v(1.09, -10.64) * mm, "end": v(1.05, -10.6) * mm});
            skLineSegment(sketch, "E384", {"start": v(1.05, -10.6) * mm, "end": v(1, -10.55) * mm});
            skLineSegment(sketch, "E385", {"start": v(1, -10.55) * mm, "end": v(0.93, -10.5) * mm});
            skLineSegment(sketch, "E386", {"start": v(0.93, -10.5) * mm, "end": v(0, -10.5) * mm});
            skLineSegment(sketch, "E387", {"start": v(0, -10.5) * mm, "end": v(-0.93, -10.5) * mm});
            skLineSegment(sketch, "E388", {"start": v(-0.93, -10.5) * mm, "end": v(-1, -10.55) * mm});
            skLineSegment(sketch, "E389", {"start": v(-1, -10.55) * mm, "end": v(-1.05, -10.6) * mm});
            skLineSegment(sketch, "E390", {"start": v(-1.05, -10.6) * mm, "end": v(-1.09, -10.64) * mm});
            skLineSegment(sketch, "E391", {"start": v(-1.09, -10.64) * mm, "end": v(-1.12, -10.69) * mm});
            skLineSegment(sketch, "E392", {"start": v(-1.12, -10.69) * mm, "end": v(-1.17, -10.78) * mm});
            skLineSegment(sketch, "E393", {"start": v(-1.17, -10.78) * mm, "end": v(-1.22, -10.88) * mm});
            skLineSegment(sketch, "E394", {"start": v(-1.22, -10.88) * mm, "end": v(-1.25, -10.97) * mm});
            skLineSegment(sketch, "E395", {"start": v(-1.25, -10.97) * mm, "end": v(-1.28, -11.07) * mm});
            skLineSegment(sketch, "E396", {"start": v(-1.28, -11.07) * mm, "end": v(-1.32, -11.27) * mm});
            skLineSegment(sketch, "E397", {"start": v(-1.32, -11.27) * mm, "end": v(-1.38, -11.47) * mm});
            skLineSegment(sketch, "E398", {"start": v(-1.38, -11.47) * mm, "end": v(-1.45, -11.66) * mm});
            skLineSegment(sketch, "E399", {"start": v(-1.45, -11.66) * mm, "end": v(-1.54, -11.85) * mm});
            skLineSegment(sketch, "E400", {"start": v(-1.54, -11.85) * mm, "end": v(-1.64, -12.04) * mm});
            skLineSegment(sketch, "E401", {"start": v(-1.64, -12.04) * mm, "end": v(-1.76, -12.23) * mm});
            skLineSegment(sketch, "E402", {"start": v(-1.76, -12.23) * mm, "end": v(-1.88, -12.41) * mm});
            skLineSegment(sketch, "E403", {"start": v(-1.88, -12.41) * mm, "end": v(-2.01, -12.6) * mm});
            skLineSegment(sketch, "E404", {"start": v(-2.01, -12.6) * mm, "end": v(-2.15, -12.77) * mm});
            skLineSegment(sketch, "E405", {"start": v(-2.15, -12.77) * mm, "end": v(-2.3, -12.95) * mm});
            skLineSegment(sketch, "E406", {"start": v(-2.3, -12.95) * mm, "end": v(-2.46, -13.13) * mm});
            skLineSegment(sketch, "E407", {"start": v(-2.46, -13.13) * mm, "end": v(-2.58, -13.26) * mm});
            skLineSegment(sketch, "E408", {"start": v(-2.58, -13.26) * mm, "end": v(-4.4, -12.77) * mm});
            skLineSegment(sketch, "E409", {"start": v(-4.4, -12.77) * mm, "end": v(-4.43, -12.6) * mm});
            skLineSegment(sketch, "E410", {"start": v(-4.43, -12.6) * mm, "end": v(-4.48, -12.37) * mm});
            skLineSegment(sketch, "E411", {"start": v(-4.48, -12.37) * mm, "end": v(-4.52, -12.14) * mm});
            skLineSegment(sketch, "E412", {"start": v(-4.52, -12.14) * mm, "end": v(-4.56, -11.91) * mm});
            skLineSegment(sketch, "E413", {"start": v(-4.56, -11.91) * mm, "end": v(-4.58, -11.69) * mm});
            skLineSegment(sketch, "E414", {"start": v(-4.58, -11.69) * mm, "end": v(-4.6, -11.47) * mm});
            skLineSegment(sketch, "E415", {"start": v(-4.6, -11.47) * mm, "end": v(-4.6, -11.25) * mm});
            skLineSegment(sketch, "E416", {"start": v(-4.6, -11.25) * mm, "end": v(-4.59, -11.03) * mm});
            skLineSegment(sketch, "E417", {"start": v(-4.59, -11.03) * mm, "end": v(-4.57, -10.82) * mm});
            skLineSegment(sketch, "E418", {"start": v(-4.57, -10.82) * mm, "end": v(-4.54, -10.62) * mm});
            skLineSegment(sketch, "E419", {"start": v(-4.54, -10.62) * mm, "end": v(-4.5, -10.42) * mm});
            skLineSegment(sketch, "E420", {"start": v(-4.5, -10.42) * mm, "end": v(-4.43, -10.23) * mm});
            skLineSegment(sketch, "E421", {"start": v(-4.43, -10.23) * mm, "end": v(-4.4, -10.13) * mm});
            skLineSegment(sketch, "E422", {"start": v(-4.4, -10.13) * mm, "end": v(-4.38, -10.03) * mm});
            skLineSegment(sketch, "E423", {"start": v(-4.38, -10.03) * mm, "end": v(-4.37, -9.92) * mm});
            skLineSegment(sketch, "E424", {"start": v(-4.37, -9.92) * mm, "end": v(-4.37, -9.81) * mm});
            skLineSegment(sketch, "E425", {"start": v(-4.37, -9.81) * mm, "end": v(-4.38, -9.76) * mm});
            skLineSegment(sketch, "E426", {"start": v(-4.38, -9.76) * mm, "end": v(-4.39, -9.7) * mm});
            skLineSegment(sketch, "E427", {"start": v(-4.39, -9.7) * mm, "end": v(-4.4, -9.63) * mm});
            skLineSegment(sketch, "E428", {"start": v(-4.4, -9.63) * mm, "end": v(-4.44, -9.56) * mm});
            skLineSegment(sketch, "E429", {"start": v(-4.44, -9.56) * mm, "end": v(-5.25, -9.09) * mm});
            skLineSegment(sketch, "E430", {"start": v(-5.25, -9.09) * mm, "end": v(-6.06, -8.63) * mm});
            skLineSegment(sketch, "E431", {"start": v(-6.06, -8.63) * mm, "end": v(-6.14, -8.63) * mm});
            skLineSegment(sketch, "E432", {"start": v(-6.14, -8.63) * mm, "end": v(-6.2, -8.65) * mm});
            skLineSegment(sketch, "E433", {"start": v(-6.2, -8.65) * mm, "end": v(-6.26, -8.67) * mm});
            skLineSegment(sketch, "E434", {"start": v(-6.26, -8.67) * mm, "end": v(-6.31, -8.7) * mm});
            skLineSegment(sketch, "E435", {"start": v(-6.31, -8.7) * mm, "end": v(-6.4, -8.75) * mm});
            skLineSegment(sketch, "E436", {"start": v(-6.4, -8.75) * mm, "end": v(-6.5, -8.81) * mm});
            skLineSegment(sketch, "E437", {"start": v(-6.5, -8.81) * mm, "end": v(-6.57, -8.88) * mm});
            skLineSegment(sketch, "E438", {"start": v(-6.57, -8.88) * mm, "end": v(-6.64, -8.95) * mm});
            skLineSegment(sketch, "E439", {"start": v(-6.64, -8.95) * mm, "end": v(-6.78, -9.1) * mm});
            skLineSegment(sketch, "E440", {"start": v(-6.78, -9.1) * mm, "end": v(-6.92, -9.24) * mm});
            skLineSegment(sketch, "E441", {"start": v(-6.92, -9.24) * mm, "end": v(-7.09, -9.37) * mm});
            skLineSegment(sketch, "E442", {"start": v(-7.09, -9.37) * mm, "end": v(-7.26, -9.5) * mm});
            skLineSegment(sketch, "E443", {"start": v(-7.26, -9.5) * mm, "end": v(-7.44, -9.6) * mm});
            skLineSegment(sketch, "E444", {"start": v(-7.44, -9.6) * mm, "end": v(-7.63, -9.71) * mm});
            skLineSegment(sketch, "E445", {"start": v(-7.63, -9.71) * mm, "end": v(-7.83, -9.8) * mm});
            skLineSegment(sketch, "E446", {"start": v(-7.83, -9.8) * mm, "end": v(-8.04, -9.9) * mm});
            skLineSegment(sketch, "E447", {"start": v(-8.04, -9.9) * mm, "end": v(-8.25, -9.99) * mm});
            skLineSegment(sketch, "E448", {"start": v(-8.25, -9.99) * mm, "end": v(-8.47, -10.07) * mm});
            skLineSegment(sketch, "E449", {"start": v(-8.47, -10.07) * mm, "end": v(-8.7, -10.14) * mm});
            skLineSegment(sketch, "E450", {"start": v(-8.7, -10.14) * mm, "end": v(-8.87, -10.19) * mm});
            skLineSegment(sketch, "E451", {"start": v(-8.87, -10.19) * mm, "end": v(-10.2, -8.87) * mm});
            skLineSegment(sketch, "E452", {"start": v(-10.2, -8.87) * mm, "end": v(-10.14, -8.7) * mm});
            skLineSegment(sketch, "E453", {"start": v(-10.14, -8.7) * mm, "end": v(-10.07, -8.47) * mm});
            skLineSegment(sketch, "E454", {"start": v(-10.07, -8.47) * mm, "end": v(-9.99, -8.25) * mm});
            skLineSegment(sketch, "E455", {"start": v(-9.99, -8.25) * mm, "end": v(-9.9, -8.04) * mm});
            skLineSegment(sketch, "E456", {"start": v(-9.9, -8.04) * mm, "end": v(-9.8, -7.83) * mm});
            skLineSegment(sketch, "E457", {"start": v(-9.8, -7.83) * mm, "end": v(-9.71, -7.63) * mm});
            skLineSegment(sketch, "E458", {"start": v(-9.71, -7.63) * mm, "end": v(-9.6, -7.44) * mm});
            skLineSegment(sketch, "E459", {"start": v(-9.6, -7.44) * mm, "end": v(-9.5, -7.26) * mm});
            skLineSegment(sketch, "E460", {"start": v(-9.5, -7.26) * mm, "end": v(-9.37, -7.09) * mm});
            skLineSegment(sketch, "E461", {"start": v(-9.37, -7.09) * mm, "end": v(-9.24, -6.92) * mm});
            skLineSegment(sketch, "E462", {"start": v(-9.24, -6.92) * mm, "end": v(-9.1, -6.78) * mm});
            skLineSegment(sketch, "E463", {"start": v(-9.1, -6.78) * mm, "end": v(-8.95, -6.64) * mm});
            skLineSegment(sketch, "E464", {"start": v(-8.95, -6.64) * mm, "end": v(-8.88, -6.57) * mm});
            skLineSegment(sketch, "E465", {"start": v(-8.88, -6.57) * mm, "end": v(-8.81, -6.5) * mm});
            skLineSegment(sketch, "E466", {"start": v(-8.81, -6.5) * mm, "end": v(-8.75, -6.4) * mm});
            skLineSegment(sketch, "E467", {"start": v(-8.75, -6.4) * mm, "end": v(-8.7, -6.31) * mm});
            skLineSegment(sketch, "E468", {"start": v(-8.7, -6.31) * mm, "end": v(-8.67, -6.26) * mm});
            skLineSegment(sketch, "E469", {"start": v(-8.67, -6.26) * mm, "end": v(-8.65, -6.2) * mm});
            skLineSegment(sketch, "E470", {"start": v(-8.65, -6.2) * mm, "end": v(-8.63, -6.14) * mm});
            skLineSegment(sketch, "E471", {"start": v(-8.63, -6.14) * mm, "end": v(-8.63, -6.06) * mm});
            skLineSegment(sketch, "E472", {"start": v(-8.63, -6.06) * mm, "end": v(-9.09, -5.25) * mm});
            skLineSegment(sketch, "E473", {"start": v(-9.09, -5.25) * mm, "end": v(-9.56, -4.44) * mm});
            skLineSegment(sketch, "E474", {"start": v(-9.56, -4.44) * mm, "end": v(-9.63, -4.4) * mm});
            skLineSegment(sketch, "E475", {"start": v(-9.63, -4.4) * mm, "end": v(-9.7, -4.39) * mm});
            skLineSegment(sketch, "E476", {"start": v(-9.7, -4.39) * mm, "end": v(-9.76, -4.38) * mm});
            skLineSegment(sketch, "E477", {"start": v(-9.76, -4.38) * mm, "end": v(-9.81, -4.37) * mm});
            skLineSegment(sketch, "E478", {"start": v(-9.81, -4.37) * mm, "end": v(-9.92, -4.37) * mm});
            skLineSegment(sketch, "E479", {"start": v(-9.92, -4.37) * mm, "end": v(-10.03, -4.38) * mm});
            skLineSegment(sketch, "E480", {"start": v(-10.03, -4.38) * mm, "end": v(-10.13, -4.4) * mm});
            skLineSegment(sketch, "E481", {"start": v(-10.13, -4.4) * mm, "end": v(-10.23, -4.43) * mm});
            skLineSegment(sketch, "E482", {"start": v(-10.23, -4.43) * mm, "end": v(-10.42, -4.5) * mm});
            skLineSegment(sketch, "E483", {"start": v(-10.42, -4.5) * mm, "end": v(-10.62, -4.54) * mm});
            skLineSegment(sketch, "E484", {"start": v(-10.62, -4.54) * mm, "end": v(-10.82, -4.57) * mm});
            skLineSegment(sketch, "E485", {"start": v(-10.82, -4.57) * mm, "end": v(-11.03, -4.59) * mm});
            skLineSegment(sketch, "E486", {"start": v(-11.03, -4.59) * mm, "end": v(-11.25, -4.6) * mm});
            skLineSegment(sketch, "E487", {"start": v(-11.25, -4.6) * mm, "end": v(-11.47, -4.6) * mm});
            skLineSegment(sketch, "E488", {"start": v(-11.47, -4.6) * mm, "end": v(-11.69, -4.58) * mm});
            skLineSegment(sketch, "E489", {"start": v(-11.69, -4.58) * mm, "end": v(-11.91, -4.56) * mm});
            skLineSegment(sketch, "E490", {"start": v(-11.91, -4.56) * mm, "end": v(-12.14, -4.52) * mm});
            skLineSegment(sketch, "E491", {"start": v(-12.14, -4.52) * mm, "end": v(-12.37, -4.48) * mm});
            skLineSegment(sketch, "E492", {"start": v(-12.37, -4.48) * mm, "end": v(-12.6, -4.43) * mm});
            skLineSegment(sketch, "E493", {"start": v(-12.6, -4.43) * mm, "end": v(-12.77, -4.4) * mm});
            skLineSegment(sketch, "E494", {"start": v(-12.77, -4.4) * mm, "end": v(-13.26, -2.58) * mm});
            skLineSegment(sketch, "E495", {"start": v(-13.26, -2.58) * mm, "end": v(-13.13, -2.46) * mm});
            skLineSegment(sketch, "E496", {"start": v(-13.13, -2.46) * mm, "end": v(-12.95, -2.3) * mm});
            skLineSegment(sketch, "E497", {"start": v(-12.95, -2.3) * mm, "end": v(-12.77, -2.15) * mm});
            skLineSegment(sketch, "E498", {"start": v(-12.77, -2.15) * mm, "end": v(-12.6, -2.01) * mm});
            skLineSegment(sketch, "E499", {"start": v(-12.6, -2.01) * mm, "end": v(-12.41, -1.88) * mm});
            skLineSegment(sketch, "E500", {"start": v(-12.41, -1.88) * mm, "end": v(-12.23, -1.76) * mm});
            skLineSegment(sketch, "E501", {"start": v(-12.23, -1.76) * mm, "end": v(-12.04, -1.64) * mm});
            skLineSegment(sketch, "E502", {"start": v(-12.04, -1.64) * mm, "end": v(-11.85, -1.54) * mm});
            skLineSegment(sketch, "E503", {"start": v(-11.85, -1.54) * mm, "end": v(-11.66, -1.45) * mm});
            skLineSegment(sketch, "E504", {"start": v(-11.66, -1.45) * mm, "end": v(-11.47, -1.38) * mm});
            skLineSegment(sketch, "E505", {"start": v(-11.47, -1.38) * mm, "end": v(-11.27, -1.32) * mm});
            skLineSegment(sketch, "E506", {"start": v(-11.27, -1.32) * mm, "end": v(-11.07, -1.28) * mm});
            skLineSegment(sketch, "E507", {"start": v(-11.07, -1.28) * mm, "end": v(-10.97, -1.25) * mm});
            skLineSegment(sketch, "E508", {"start": v(-10.97, -1.25) * mm, "end": v(-10.88, -1.22) * mm});
            skLineSegment(sketch, "E509", {"start": v(-10.88, -1.22) * mm, "end": v(-10.78, -1.17) * mm});
            skLineSegment(sketch, "E510", {"start": v(-10.78, -1.17) * mm, "end": v(-10.69, -1.12) * mm});
            skLineSegment(sketch, "E511", {"start": v(-10.69, -1.12) * mm, "end": v(-10.64, -1.09) * mm});
            skLineSegment(sketch, "E512", {"start": v(-10.64, -1.09) * mm, "end": v(-10.6, -1.05) * mm});
            skLineSegment(sketch, "E513", {"start": v(-10.6, -1.05) * mm, "end": v(-10.55, -1) * mm});
            skLineSegment(sketch, "E514", {"start": v(-10.55, -1) * mm, "end": v(-10.5, -0.93) * mm});
            skLineSegment(sketch, "E515", {"start": v(-10.5, -0.93) * mm, "end": v(-10.5, 0) * mm});
            skPoint(sketch, "E516", {"position": v(0, 0) * mm});
            skSolve(sketch);
        }
        {
            var Q0;
            Q0=makeQuery(id+"F0.imprint","IMPRINT",FACE,{"disambiguationData":[TD([[makeQuery(id+"F0.imprint","IMPRINT",EDGE,{"derivedFrom":sQuery(id+"F0.wireOp",EDGE,"E0")}),-1.0]])]});
            extrude(context, id + "F1", {"entities" : qUnion([Q0]), "depth" : 3 * mm});
        }
        {
            var Q0;
            Q0=makeQuery(id+"F1.opExtrude","CAP_FACE",FACE,{"disambiguationData":[OSD([sQuery(id+"F0.wireOp",EDGE,"E0"),sQuery(id+"F0.wireOp",EDGE,"E1"),sQuery(id+"F0.wireOp",EDGE,"E2"),sQuery(id+"F0.wireOp",EDGE,"E3"),sQuery(id+"F0.wireOp",EDGE,"E4"),sQuery(id+"F0.wireOp",EDGE,"E5"),sQuery(id+"F0.wireOp",EDGE,"E6"),sQuery(id+"F0.wireOp",EDGE,"E7"),sQuery(id+"F0.wireOp",EDGE,"E8"),sQuery(id+"F0.wireOp",EDGE,"E9"),sQuery(id+"F0.wireOp",EDGE,"E10"),sQuery(id+"F0.wireOp",EDGE,"E11"),sQuery(id+"F0.wireOp",EDGE,"E12"),sQuery(id+"F0.wireOp",EDGE,"E13"),sQuery(id+"F0.wireOp",EDGE,"E14"),sQuery(id+"F0.wireOp",EDGE,"E15"),sQuery(id+"F0.wireOp",EDGE,"E16"),sQuery(id+"F0.wireOp",EDGE,"E17"),sQuery(id+"F0.wireOp",EDGE,"E18"),sQuery(id+"F0.wireOp",EDGE,"E19"),sQuery(id+"F0.wireOp",EDGE,"E20"),sQuery(id+"F0.wireOp",EDGE,"E21"),sQuery(id+"F0.wireOp",EDGE,"E22"),sQuery(id+"F0.wireOp",EDGE,"E23"),sQuery(id+"F0.wireOp",EDGE,"E24"),sQuery(id+"F0.wireOp",EDGE,"E25"),sQuery(id+"F0.wireOp",EDGE,"E26"),sQuery(id+"F0.wireOp",EDGE,"E27"),sQuery(id+"F0.wireOp",EDGE,"E28"),sQuery(id+"F0.wireOp",EDGE,"E29"),sQuery(id+"F0.wireOp",EDGE,"E30"),sQuery(id+"F0.wireOp",EDGE,"E31"),sQuery(id+"F0.wireOp",EDGE,"E32"),sQuery(id+"F0.wireOp",EDGE,"E33"),sQuery(id+"F0.wireOp",EDGE,"E34"),sQuery(id+"F0.wireOp",EDGE,"E35"),sQuery(id+"F0.wireOp",EDGE,"E36"),sQuery(id+"F0.wireOp",EDGE,"E37"),sQuery(id+"F0.wireOp",EDGE,"E38"),sQuery(id+"F0.wireOp",EDGE,"E39"),sQuery(id+"F0.wireOp",EDGE,"E40"),sQuery(id+"F0.wireOp",EDGE,"E41"),sQuery(id+"F0.wireOp",EDGE,"E42"),sQuery(id+"F0.wireOp",EDGE,"E43"),sQuery(id+"F0.wireOp",EDGE,"E44"),sQuery(id+"F0.wireOp",EDGE,"E45"),sQuery(id+"F0.wireOp",EDGE,"E46"),sQuery(id+"F0.wireOp",EDGE,"E47"),sQuery(id+"F0.wireOp",EDGE,"E48"),sQuery(id+"F0.wireOp",EDGE,"E49"),sQuery(id+"F0.wireOp",EDGE,"E50"),sQuery(id+"F0.wireOp",EDGE,"E51"),sQuery(id+"F0.wireOp",EDGE,"E52"),sQuery(id+"F0.wireOp",EDGE,"E53"),sQuery(id+"F0.wireOp",EDGE,"E54"),sQuery(id+"F0.wireOp",EDGE,"E55"),sQuery(id+"F0.wireOp",EDGE,"E56"),sQuery(id+"F0.wireOp",EDGE,"E57"),sQuery(id+"F0.wireOp",EDGE,"E58"),sQuery(id+"F0.wireOp",EDGE,"E59"),sQuery(id+"F0.wireOp",EDGE,"E60"),sQuery(id+"F0.wireOp",EDGE,"E61"),sQuery(id+"F0.wireOp",EDGE,"E62"),sQuery(id+"F0.wireOp",EDGE,"E63"),sQuery(id+"F0.wireOp",EDGE,"E64"),sQuery(id+"F0.wireOp",EDGE,"E65"),sQuery(id+"F0.wireOp",EDGE,"E66"),sQuery(id+"F0.wireOp",EDGE,"E67"),sQuery(id+"F0.wireOp",EDGE,"E68"),sQuery(id+"F0.wireOp",EDGE,"E69"),sQuery(id+"F0.wireOp",EDGE,"E70"),sQuery(id+"F0.wireOp",EDGE,"E71"),sQuery(id+"F0.wireOp",EDGE,"E72"),sQuery(id+"F0.wireOp",EDGE,"E73"),sQuery(id+"F0.wireOp",EDGE,"E74"),sQuery(id+"F0.wireOp",EDGE,"E75"),sQuery(id+"F0.wireOp",EDGE,"E76"),sQuery(id+"F0.wireOp",EDGE,"E77"),sQuery(id+"F0.wireOp",EDGE,"E78"),sQuery(id+"F0.wireOp",EDGE,"E79"),sQuery(id+"F0.wireOp",EDGE,"E80"),sQuery(id+"F0.wireOp",EDGE,"E81"),sQuery(id+"F0.wireOp",EDGE,"E82"),sQuery(id+"F0.wireOp",EDGE,"E83"),sQuery(id+"F0.wireOp",EDGE,"E84"),sQuery(id+"F0.wireOp",EDGE,"E85"),sQuery(id+"F0.wireOp",EDGE,"E86"),sQuery(id+"F0.wireOp",EDGE,"E87"),sQuery(id+"F0.wireOp",EDGE,"E88"),sQuery(id+"F0.wireOp",EDGE,"E89"),sQuery(id+"F0.wireOp",EDGE,"E90"),sQuery(id+"F0.wireOp",EDGE,"E91"),sQuery(id+"F0.wireOp",EDGE,"E92"),sQuery(id+"F0.wireOp",EDGE,"E93"),sQuery(id+"F0.wireOp",EDGE,"E94"),sQuery(id+"F0.wireOp",EDGE,"E95"),sQuery(id+"F0.wireOp",EDGE,"E96"),sQuery(id+"F0.wireOp",EDGE,"E97"),sQuery(id+"F0.wireOp",EDGE,"E98"),sQuery(id+"F0.wireOp",EDGE,"E99"),sQuery(id+"F0.wireOp",EDGE,"E100"),sQuery(id+"F0.wireOp",EDGE,"E101"),sQuery(id+"F0.wireOp",EDGE,"E102"),sQuery(id+"F0.wireOp",EDGE,"E103"),sQuery(id+"F0.wireOp",EDGE,"E104"),sQuery(id+"F0.wireOp",EDGE,"E105"),sQuery(id+"F0.wireOp",EDGE,"E106"),sQuery(id+"F0.wireOp",EDGE,"E107"),sQuery(id+"F0.wireOp",EDGE,"E108"),sQuery(id+"F0.wireOp",EDGE,"E109"),sQuery(id+"F0.wireOp",EDGE,"E110"),sQuery(id+"F0.wireOp",EDGE,"E111"),sQuery(id+"F0.wireOp",EDGE,"E112"),sQuery(id+"F0.wireOp",EDGE,"E113"),sQuery(id+"F0.wireOp",EDGE,"E114"),sQuery(id+"F0.wireOp",EDGE,"E115"),sQuery(id+"F0.wireOp",EDGE,"E116"),sQuery(id+"F0.wireOp",EDGE,"E117"),sQuery(id+"F0.wireOp",EDGE,"E118"),sQuery(id+"F0.wireOp",EDGE,"E119"),sQuery(id+"F0.wireOp",EDGE,"E120"),sQuery(id+"F0.wireOp",EDGE,"E121"),sQuery(id+"F0.wireOp",EDGE,"E122"),sQuery(id+"F0.wireOp",EDGE,"E123"),sQuery(id+"F0.wireOp",EDGE,"E124"),sQuery(id+"F0.wireOp",EDGE,"E125"),sQuery(id+"F0.wireOp",EDGE,"E126"),sQuery(id+"F0.wireOp",EDGE,"E127"),sQuery(id+"F0.wireOp",EDGE,"E128"),sQuery(id+"F0.wireOp",EDGE,"E129"),sQuery(id+"F0.wireOp",EDGE,"E130"),sQuery(id+"F0.wireOp",EDGE,"E131"),sQuery(id+"F0.wireOp",EDGE,"E132"),sQuery(id+"F0.wireOp",EDGE,"E133"),sQuery(id+"F0.wireOp",EDGE,"E134"),sQuery(id+"F0.wireOp",EDGE,"E135"),sQuery(id+"F0.wireOp",EDGE,"E136"),sQuery(id+"F0.wireOp",EDGE,"E137"),sQuery(id+"F0.wireOp",EDGE,"E138"),sQuery(id+"F0.wireOp",EDGE,"E139"),sQuery(id+"F0.wireOp",EDGE,"E140"),sQuery(id+"F0.wireOp",EDGE,"E141"),sQuery(id+"F0.wireOp",EDGE,"E142"),sQuery(id+"F0.wireOp",EDGE,"E143"),sQuery(id+"F0.wireOp",EDGE,"E144"),sQuery(id+"F0.wireOp",EDGE,"E145"),sQuery(id+"F0.wireOp",EDGE,"E146"),sQuery(id+"F0.wireOp",EDGE,"E147"),sQuery(id+"F0.wireOp",EDGE,"E148"),sQuery(id+"F0.wireOp",EDGE,"E149"),sQuery(id+"F0.wireOp",EDGE,"E150"),sQuery(id+"F0.wireOp",EDGE,"E151"),sQuery(id+"F0.wireOp",EDGE,"E152"),sQuery(id+"F0.wireOp",EDGE,"E153"),sQuery(id+"F0.wireOp",EDGE,"E154"),sQuery(id+"F0.wireOp",EDGE,"E155"),sQuery(id+"F0.wireOp",EDGE,"E156"),sQuery(id+"F0.wireOp",EDGE,"E157"),sQuery(id+"F0.wireOp",EDGE,"E158"),sQuery(id+"F0.wireOp",EDGE,"E159"),sQuery(id+"F0.wireOp",EDGE,"E160"),sQuery(id+"F0.wireOp",EDGE,"E161"),sQuery(id+"F0.wireOp",EDGE,"E162"),sQuery(id+"F0.wireOp",EDGE,"E163"),sQuery(id+"F0.wireOp",EDGE,"E164"),sQuery(id+"F0.wireOp",EDGE,"E165"),sQuery(id+"F0.wireOp",EDGE,"E166"),sQuery(id+"F0.wireOp",EDGE,"E167"),sQuery(id+"F0.wireOp",EDGE,"E168"),sQuery(id+"F0.wireOp",EDGE,"E169"),sQuery(id+"F0.wireOp",EDGE,"E170"),sQuery(id+"F0.wireOp",EDGE,"E171"),sQuery(id+"F0.wireOp",EDGE,"E172"),sQuery(id+"F0.wireOp",EDGE,"E173"),sQuery(id+"F0.wireOp",EDGE,"E174"),sQuery(id+"F0.wireOp",EDGE,"E175"),sQuery(id+"F0.wireOp",EDGE,"E176"),sQuery(id+"F0.wireOp",EDGE,"E177"),sQuery(id+"F0.wireOp",EDGE,"E178"),sQuery(id+"F0.wireOp",EDGE,"E179"),sQuery(id+"F0.wireOp",EDGE,"E180"),sQuery(id+"F0.wireOp",EDGE,"E181"),sQuery(id+"F0.wireOp",EDGE,"E182"),sQuery(id+"F0.wireOp",EDGE,"E183"),sQuery(id+"F0.wireOp",EDGE,"E184"),sQuery(id+"F0.wireOp",EDGE,"E185"),sQuery(id+"F0.wireOp",EDGE,"E186"),sQuery(id+"F0.wireOp",EDGE,"E187"),sQuery(id+"F0.wireOp",EDGE,"E188"),sQuery(id+"F0.wireOp",EDGE,"E189"),sQuery(id+"F0.wireOp",EDGE,"E190"),sQuery(id+"F0.wireOp",EDGE,"E191"),sQuery(id+"F0.wireOp",EDGE,"E192"),sQuery(id+"F0.wireOp",EDGE,"E193"),sQuery(id+"F0.wireOp",EDGE,"E194"),sQuery(id+"F0.wireOp",EDGE,"E195"),sQuery(id+"F0.wireOp",EDGE,"E196"),sQuery(id+"F0.wireOp",EDGE,"E197"),sQuery(id+"F0.wireOp",EDGE,"E198"),sQuery(id+"F0.wireOp",EDGE,"E199"),sQuery(id+"F0.wireOp",EDGE,"E200"),sQuery(id+"F0.wireOp",EDGE,"E201"),sQuery(id+"F0.wireOp",EDGE,"E202"),sQuery(id+"F0.wireOp",EDGE,"E203"),sQuery(id+"F0.wireOp",EDGE,"E204"),sQuery(id+"F0.wireOp",EDGE,"E205"),sQuery(id+"F0.wireOp",EDGE,"E206"),sQuery(id+"F0.wireOp",EDGE,"E207"),sQuery(id+"F0.wireOp",EDGE,"E208"),sQuery(id+"F0.wireOp",EDGE,"E209"),sQuery(id+"F0.wireOp",EDGE,"E210"),sQuery(id+"F0.wireOp",EDGE,"E211"),sQuery(id+"F0.wireOp",EDGE,"E212"),sQuery(id+"F0.wireOp",EDGE,"E213"),sQuery(id+"F0.wireOp",EDGE,"E214"),sQuery(id+"F0.wireOp",EDGE,"E215"),sQuery(id+"F0.wireOp",EDGE,"E216"),sQuery(id+"F0.wireOp",EDGE,"E217"),sQuery(id+"F0.wireOp",EDGE,"E218"),sQuery(id+"F0.wireOp",EDGE,"E219"),sQuery(id+"F0.wireOp",EDGE,"E220"),sQuery(id+"F0.wireOp",EDGE,"E221"),sQuery(id+"F0.wireOp",EDGE,"E222"),sQuery(id+"F0.wireOp",EDGE,"E223"),sQuery(id+"F0.wireOp",EDGE,"E224"),sQuery(id+"F0.wireOp",EDGE,"E225"),sQuery(id+"F0.wireOp",EDGE,"E226"),sQuery(id+"F0.wireOp",EDGE,"E227"),sQuery(id+"F0.wireOp",EDGE,"E228"),sQuery(id+"F0.wireOp",EDGE,"E229"),sQuery(id+"F0.wireOp",EDGE,"E230"),sQuery(id+"F0.wireOp",EDGE,"E231"),sQuery(id+"F0.wireOp",EDGE,"E232"),sQuery(id+"F0.wireOp",EDGE,"E233"),sQuery(id+"F0.wireOp",EDGE,"E234"),sQuery(id+"F0.wireOp",EDGE,"E235"),sQuery(id+"F0.wireOp",EDGE,"E236"),sQuery(id+"F0.wireOp",EDGE,"E237"),sQuery(id+"F0.wireOp",EDGE,"E238"),sQuery(id+"F0.wireOp",EDGE,"E239"),sQuery(id+"F0.wireOp",EDGE,"E240"),sQuery(id+"F0.wireOp",EDGE,"E241"),sQuery(id+"F0.wireOp",EDGE,"E242"),sQuery(id+"F0.wireOp",EDGE,"E243"),sQuery(id+"F0.wireOp",EDGE,"E244"),sQuery(id+"F0.wireOp",EDGE,"E245"),sQuery(id+"F0.wireOp",EDGE,"E246"),sQuery(id+"F0.wireOp",EDGE,"E247"),sQuery(id+"F0.wireOp",EDGE,"E248"),sQuery(id+"F0.wireOp",EDGE,"E249"),sQuery(id+"F0.wireOp",EDGE,"E250"),sQuery(id+"F0.wireOp",EDGE,"E251"),sQuery(id+"F0.wireOp",EDGE,"E252"),sQuery(id+"F0.wireOp",EDGE,"E253"),sQuery(id+"F0.wireOp",EDGE,"E254"),sQuery(id+"F0.wireOp",EDGE,"E255"),sQuery(id+"F0.wireOp",EDGE,"E256"),sQuery(id+"F0.wireOp",EDGE,"E257"),sQuery(id+"F0.wireOp",EDGE,"E258"),sQuery(id+"F0.wireOp",EDGE,"E259"),sQuery(id+"F0.wireOp",EDGE,"E260"),sQuery(id+"F0.wireOp",EDGE,"E261"),sQuery(id+"F0.wireOp",EDGE,"E262"),sQuery(id+"F0.wireOp",EDGE,"E263"),sQuery(id+"F0.wireOp",EDGE,"E264"),sQuery(id+"F0.wireOp",EDGE,"E265"),sQuery(id+"F0.wireOp",EDGE,"E266"),sQuery(id+"F0.wireOp",EDGE,"E267"),sQuery(id+"F0.wireOp",EDGE,"E268"),sQuery(id+"F0.wireOp",EDGE,"E269"),sQuery(id+"F0.wireOp",EDGE,"E270"),sQuery(id+"F0.wireOp",EDGE,"E271"),sQuery(id+"F0.wireOp",EDGE,"E272"),sQuery(id+"F0.wireOp",EDGE,"E273"),sQuery(id+"F0.wireOp",EDGE,"E274"),sQuery(id+"F0.wireOp",EDGE,"E275"),sQuery(id+"F0.wireOp",EDGE,"E276"),sQuery(id+"F0.wireOp",EDGE,"E277"),sQuery(id+"F0.wireOp",EDGE,"E278"),sQuery(id+"F0.wireOp",EDGE,"E279"),sQuery(id+"F0.wireOp",EDGE,"E280"),sQuery(id+"F0.wireOp",EDGE,"E281"),sQuery(id+"F0.wireOp",EDGE,"E282"),sQuery(id+"F0.wireOp",EDGE,"E283"),sQuery(id+"F0.wireOp",EDGE,"E284"),sQuery(id+"F0.wireOp",EDGE,"E285"),sQuery(id+"F0.wireOp",EDGE,"E286"),sQuery(id+"F0.wireOp",EDGE,"E287"),sQuery(id+"F0.wireOp",EDGE,"E288"),sQuery(id+"F0.wireOp",EDGE,"E289"),sQuery(id+"F0.wireOp",EDGE,"E290"),sQuery(id+"F0.wireOp",EDGE,"E291"),sQuery(id+"F0.wireOp",EDGE,"E292"),sQuery(id+"F0.wireOp",EDGE,"E293"),sQuery(id+"F0.wireOp",EDGE,"E294"),sQuery(id+"F0.wireOp",EDGE,"E295"),sQuery(id+"F0.wireOp",EDGE,"E296"),sQuery(id+"F0.wireOp",EDGE,"E297"),sQuery(id+"F0.wireOp",EDGE,"E298"),sQuery(id+"F0.wireOp",EDGE,"E299"),sQuery(id+"F0.wireOp",EDGE,"E300"),sQuery(id+"F0.wireOp",EDGE,"E301"),sQuery(id+"F0.wireOp",EDGE,"E302"),sQuery(id+"F0.wireOp",EDGE,"E303"),sQuery(id+"F0.wireOp",EDGE,"E304"),sQuery(id+"F0.wireOp",EDGE,"E305"),sQuery(id+"F0.wireOp",EDGE,"E306"),sQuery(id+"F0.wireOp",EDGE,"E307"),sQuery(id+"F0.wireOp",EDGE,"E308"),sQuery(id+"F0.wireOp",EDGE,"E309"),sQuery(id+"F0.wireOp",EDGE,"E310"),sQuery(id+"F0.wireOp",EDGE,"E311"),sQuery(id+"F0.wireOp",EDGE,"E312"),sQuery(id+"F0.wireOp",EDGE,"E313"),sQuery(id+"F0.wireOp",EDGE,"E314"),sQuery(id+"F0.wireOp",EDGE,"E315"),sQuery(id+"F0.wireOp",EDGE,"E316"),sQuery(id+"F0.wireOp",EDGE,"E317"),sQuery(id+"F0.wireOp",EDGE,"E318"),sQuery(id+"F0.wireOp",EDGE,"E319"),sQuery(id+"F0.wireOp",EDGE,"E320"),sQuery(id+"F0.wireOp",EDGE,"E321"),sQuery(id+"F0.wireOp",EDGE,"E322"),sQuery(id+"F0.wireOp",EDGE,"E323"),sQuery(id+"F0.wireOp",EDGE,"E324"),sQuery(id+"F0.wireOp",EDGE,"E325"),sQuery(id+"F0.wireOp",EDGE,"E326"),sQuery(id+"F0.wireOp",EDGE,"E327"),sQuery(id+"F0.wireOp",EDGE,"E328"),sQuery(id+"F0.wireOp",EDGE,"E329"),sQuery(id+"F0.wireOp",EDGE,"E330"),sQuery(id+"F0.wireOp",EDGE,"E331"),sQuery(id+"F0.wireOp",EDGE,"E332"),sQuery(id+"F0.wireOp",EDGE,"E333"),sQuery(id+"F0.wireOp",EDGE,"E334"),sQuery(id+"F0.wireOp",EDGE,"E335"),sQuery(id+"F0.wireOp",EDGE,"E336"),sQuery(id+"F0.wireOp",EDGE,"E337"),sQuery(id+"F0.wireOp",EDGE,"E338"),sQuery(id+"F0.wireOp",EDGE,"E339"),sQuery(id+"F0.wireOp",EDGE,"E340"),sQuery(id+"F0.wireOp",EDGE,"E341"),sQuery(id+"F0.wireOp",EDGE,"E342"),sQuery(id+"F0.wireOp",EDGE,"E343"),sQuery(id+"F0.wireOp",EDGE,"E344"),sQuery(id+"F0.wireOp",EDGE,"E345"),sQuery(id+"F0.wireOp",EDGE,"E346"),sQuery(id+"F0.wireOp",EDGE,"E347"),sQuery(id+"F0.wireOp",EDGE,"E348"),sQuery(id+"F0.wireOp",EDGE,"E349"),sQuery(id+"F0.wireOp",EDGE,"E350"),sQuery(id+"F0.wireOp",EDGE,"E351"),sQuery(id+"F0.wireOp",EDGE,"E352"),sQuery(id+"F0.wireOp",EDGE,"E353"),sQuery(id+"F0.wireOp",EDGE,"E354"),sQuery(id+"F0.wireOp",EDGE,"E355"),sQuery(id+"F0.wireOp",EDGE,"E356"),sQuery(id+"F0.wireOp",EDGE,"E357"),sQuery(id+"F0.wireOp",EDGE,"E358"),sQuery(id+"F0.wireOp",EDGE,"E359"),sQuery(id+"F0.wireOp",EDGE,"E360"),sQuery(id+"F0.wireOp",EDGE,"E361"),sQuery(id+"F0.wireOp",EDGE,"E362"),sQuery(id+"F0.wireOp",EDGE,"E363"),sQuery(id+"F0.wireOp",EDGE,"E364"),sQuery(id+"F0.wireOp",EDGE,"E365"),sQuery(id+"F0.wireOp",EDGE,"E366"),sQuery(id+"F0.wireOp",EDGE,"E367"),sQuery(id+"F0.wireOp",EDGE,"E368"),sQuery(id+"F0.wireOp",EDGE,"E369"),sQuery(id+"F0.wireOp",EDGE,"E370"),sQuery(id+"F0.wireOp",EDGE,"E371"),sQuery(id+"F0.wireOp",EDGE,"E372"),sQuery(id+"F0.wireOp",EDGE,"E373"),sQuery(id+"F0.wireOp",EDGE,"E374"),sQuery(id+"F0.wireOp",EDGE,"E375"),sQuery(id+"F0.wireOp",EDGE,"E376"),sQuery(id+"F0.wireOp",EDGE,"E377"),sQuery(id+"F0.wireOp",EDGE,"E378"),sQuery(id+"F0.wireOp",EDGE,"E379"),sQuery(id+"F0.wireOp",EDGE,"E380"),sQuery(id+"F0.wireOp",EDGE,"E381"),sQuery(id+"F0.wireOp",EDGE,"E382"),sQuery(id+"F0.wireOp",EDGE,"E383"),sQuery(id+"F0.wireOp",EDGE,"E384"),sQuery(id+"F0.wireOp",EDGE,"E385"),sQuery(id+"F0.wireOp",EDGE,"E386"),sQuery(id+"F0.wireOp",EDGE,"E387"),sQuery(id+"F0.wireOp",EDGE,"E388"),sQuery(id+"F0.wireOp",EDGE,"E389"),sQuery(id+"F0.wireOp",EDGE,"E390"),sQuery(id+"F0.wireOp",EDGE,"E391"),sQuery(id+"F0.wireOp",EDGE,"E392"),sQuery(id+"F0.wireOp",EDGE,"E393"),sQuery(id+"F0.wireOp",EDGE,"E394"),sQuery(id+"F0.wireOp",EDGE,"E395"),sQuery(id+"F0.wireOp",EDGE,"E396"),sQuery(id+"F0.wireOp",EDGE,"E397"),sQuery(id+"F0.wireOp",EDGE,"E398"),sQuery(id+"F0.wireOp",EDGE,"E399"),sQuery(id+"F0.wireOp",EDGE,"E400"),sQuery(id+"F0.wireOp",EDGE,"E401"),sQuery(id+"F0.wireOp",EDGE,"E402"),sQuery(id+"F0.wireOp",EDGE,"E403"),sQuery(id+"F0.wireOp",EDGE,"E404"),sQuery(id+"F0.wireOp",EDGE,"E405"),sQuery(id+"F0.wireOp",EDGE,"E406"),sQuery(id+"F0.wireOp",EDGE,"E407"),sQuery(id+"F0.wireOp",EDGE,"E408"),sQuery(id+"F0.wireOp",EDGE,"E409"),sQuery(id+"F0.wireOp",EDGE,"E410"),sQuery(id+"F0.wireOp",EDGE,"E411"),sQuery(id+"F0.wireOp",EDGE,"E412"),sQuery(id+"F0.wireOp",EDGE,"E413"),sQuery(id+"F0.wireOp",EDGE,"E414"),sQuery(id+"F0.wireOp",EDGE,"E415"),sQuery(id+"F0.wireOp",EDGE,"E416"),sQuery(id+"F0.wireOp",EDGE,"E417"),sQuery(id+"F0.wireOp",EDGE,"E418"),sQuery(id+"F0.wireOp",EDGE,"E419"),sQuery(id+"F0.wireOp",EDGE,"E420"),sQuery(id+"F0.wireOp",EDGE,"E421"),sQuery(id+"F0.wireOp",EDGE,"E422"),sQuery(id+"F0.wireOp",EDGE,"E423"),sQuery(id+"F0.wireOp",EDGE,"E424"),sQuery(id+"F0.wireOp",EDGE,"E425"),sQuery(id+"F0.wireOp",EDGE,"E426"),sQuery(id+"F0.wireOp",EDGE,"E427"),sQuery(id+"F0.wireOp",EDGE,"E428"),sQuery(id+"F0.wireOp",EDGE,"E429"),sQuery(id+"F0.wireOp",EDGE,"E430"),sQuery(id+"F0.wireOp",EDGE,"E431"),sQuery(id+"F0.wireOp",EDGE,"E432"),sQuery(id+"F0.wireOp",EDGE,"E433"),sQuery(id+"F0.wireOp",EDGE,"E434"),sQuery(id+"F0.wireOp",EDGE,"E435"),sQuery(id+"F0.wireOp",EDGE,"E436"),sQuery(id+"F0.wireOp",EDGE,"E437"),sQuery(id+"F0.wireOp",EDGE,"E438"),sQuery(id+"F0.wireOp",EDGE,"E439"),sQuery(id+"F0.wireOp",EDGE,"E440"),sQuery(id+"F0.wireOp",EDGE,"E441"),sQuery(id+"F0.wireOp",EDGE,"E442"),sQuery(id+"F0.wireOp",EDGE,"E443"),sQuery(id+"F0.wireOp",EDGE,"E444"),sQuery(id+"F0.wireOp",EDGE,"E445"),sQuery(id+"F0.wireOp",EDGE,"E446"),sQuery(id+"F0.wireOp",EDGE,"E447"),sQuery(id+"F0.wireOp",EDGE,"E448"),sQuery(id+"F0.wireOp",EDGE,"E449"),sQuery(id+"F0.wireOp",EDGE,"E450"),sQuery(id+"F0.wireOp",EDGE,"E451"),sQuery(id+"F0.wireOp",EDGE,"E452"),sQuery(id+"F0.wireOp",EDGE,"E453"),sQuery(id+"F0.wireOp",EDGE,"E454"),sQuery(id+"F0.wireOp",EDGE,"E455"),sQuery(id+"F0.wireOp",EDGE,"E456"),sQuery(id+"F0.wireOp",EDGE,"E457"),sQuery(id+"F0.wireOp",EDGE,"E458"),sQuery(id+"F0.wireOp",EDGE,"E459"),sQuery(id+"F0.wireOp",EDGE,"E460"),sQuery(id+"F0.wireOp",EDGE,"E461"),sQuery(id+"F0.wireOp",EDGE,"E462"),sQuery(id+"F0.wireOp",EDGE,"E463"),sQuery(id+"F0.wireOp",EDGE,"E464"),sQuery(id+"F0.wireOp",EDGE,"E465"),sQuery(id+"F0.wireOp",EDGE,"E466"),sQuery(id+"F0.wireOp",EDGE,"E467"),sQuery(id+"F0.wireOp",EDGE,"E468"),sQuery(id+"F0.wireOp",EDGE,"E469"),sQuery(id+"F0.wireOp",EDGE,"E470"),sQuery(id+"F0.wireOp",EDGE,"E471"),sQuery(id+"F0.wireOp",EDGE,"E472"),sQuery(id+"F0.wireOp",EDGE,"E473"),sQuery(id+"F0.wireOp",EDGE,"E474"),sQuery(id+"F0.wireOp",EDGE,"E475"),sQuery(id+"F0.wireOp",EDGE,"E476"),sQuery(id+"F0.wireOp",EDGE,"E477"),sQuery(id+"F0.wireOp",EDGE,"E478"),sQuery(id+"F0.wireOp",EDGE,"E479"),sQuery(id+"F0.wireOp",EDGE,"E480"),sQuery(id+"F0.wireOp",EDGE,"E481"),sQuery(id+"F0.wireOp",EDGE,"E482"),sQuery(id+"F0.wireOp",EDGE,"E483"),sQuery(id+"F0.wireOp",EDGE,"E484"),sQuery(id+"F0.wireOp",EDGE,"E485"),sQuery(id+"F0.wireOp",EDGE,"E486"),sQuery(id+"F0.wireOp",EDGE,"E487"),sQuery(id+"F0.wireOp",EDGE,"E488"),sQuery(id+"F0.wireOp",EDGE,"E489"),sQuery(id+"F0.wireOp",EDGE,"E490"),sQuery(id+"F0.wireOp",EDGE,"E491"),sQuery(id+"F0.wireOp",EDGE,"E492"),sQuery(id+"F0.wireOp",EDGE,"E493"),sQuery(id+"F0.wireOp",EDGE,"E494"),sQuery(id+"F0.wireOp",EDGE,"E495"),sQuery(id+"F0.wireOp",EDGE,"E496"),sQuery(id+"F0.wireOp",EDGE,"E497"),sQuery(id+"F0.wireOp",EDGE,"E498"),sQuery(id+"F0.wireOp",EDGE,"E499"),sQuery(id+"F0.wireOp",EDGE,"E500"),sQuery(id+"F0.wireOp",EDGE,"E501"),sQuery(id+"F0.wireOp",EDGE,"E502"),sQuery(id+"F0.wireOp",EDGE,"E503"),sQuery(id+"F0.wireOp",EDGE,"E504"),sQuery(id+"F0.wireOp",EDGE,"E505"),sQuery(id+"F0.wireOp",EDGE,"E506"),sQuery(id+"F0.wireOp",EDGE,"E507"),sQuery(id+"F0.wireOp",EDGE,"E508"),sQuery(id+"F0.wireOp",EDGE,"E509"),sQuery(id+"F0.wireOp",EDGE,"E510"),sQuery(id+"F0.wireOp",EDGE,"E511"),sQuery(id+"F0.wireOp",EDGE,"E512"),sQuery(id+"F0.wireOp",EDGE,"E513"),sQuery(id+"F0.wireOp",EDGE,"E514"),sQuery(id+"F0.wireOp",EDGE,"E515")])],"isStart":false});
            var sketch = newSketch(context, id + "F2", { "sketchPlane" : qUnion([Q0])});
            skCircle(sketch, "E517", {"center": v(0, 0) * mm, "radius": 3.5 * mm});
            skSolve(sketch);
        }
        {
            var Q0;
            Q0=makeQuery(id+"F2.imprint","IMPRINT",FACE,{"disambiguationData":[TD([[makeQuery(id+"F2.imprint","IMPRINT",EDGE,{"derivedFrom":sQuery(id+"F2.wireOp",EDGE,"E517")}),1.0]])]});
            extrude(context, id + "F3", {"entities" : qUnion([Q0]), "operationType" : NewBodyOperationType.REMOVE, "endBound" : BoundingType.THROUGH_ALL, "oppositeDirection" : true, "depth" : 25 * mm});
        }
    });
